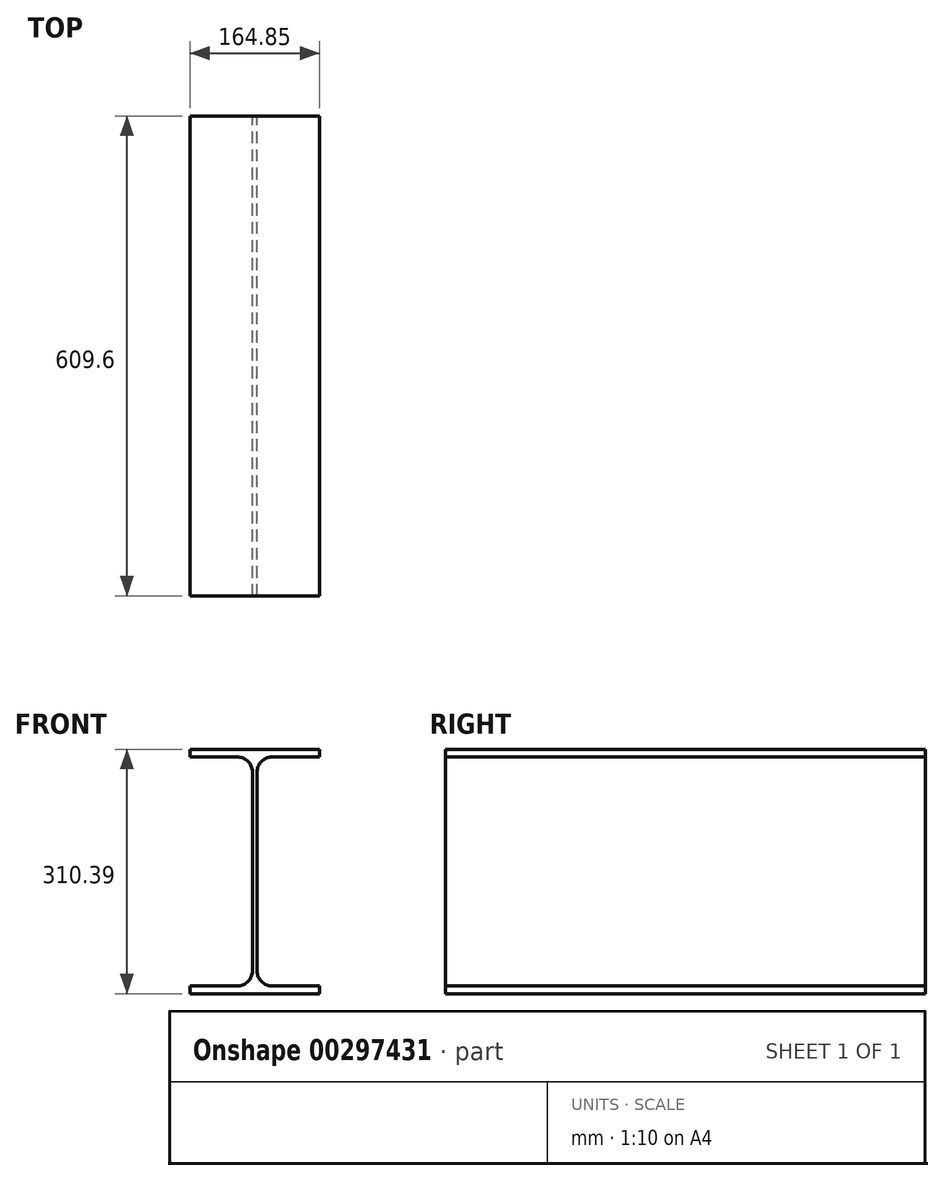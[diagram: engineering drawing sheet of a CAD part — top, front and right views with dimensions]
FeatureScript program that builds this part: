
annotation { "Feature Type Name" : "Feature", "Feature Type Description" : "" }
export const myFeature = defineFeature(function(context is Context, id is Id, definition is map)
    precondition{}
    {
        {
            var Q0;
            Q0=qCreatedBy(makeId("Front.planeOp"),FACE);
            var sketch = newSketch(context, id + "F0", { "sketchPlane" : qUnion([Q0])});
            skLineSegment(sketch, "E0", {"start": v(-2132.4, 1134.06) * mm, "end": v(-2031.56, 1134.06) * mm});
            skLineSegment(sketch, "E1", {"start": v(-2132.4, 1436.58) * mm, "end": v(-2031.56, 1436.58) * mm});
            skLineSegment(sketch, "E2", {"start": v(-2060.53, 1139.78) * mm, "end": v(-2031.56, 1139.78) * mm});
            skLineSegment(sketch, "E3", {"start": v(-2060.53, 1430.86) * mm, "end": v(-2031.56, 1430.86) * mm});
            skLineSegment(sketch, "E4", {"start": v(-2084.52, 1158.69) * mm, "end": v(-2084.52, 1411.95) * mm});
            skLineSegment(sketch, "E5", {"start": v(-2079.44, 1158.69) * mm, "end": v(-2079.44, 1411.95) * mm});
            skArc(sketch, "E6", {"start": v(-2103.42, 1139.78) * mm, "mid": v(-2090.05, 1145.32) * mm, "end": v(-2084.52, 1158.69) * mm});
            skLineSegment(sketch, "E7", {"start": v(-2132.4, 1134.06) * mm, "end": v(-2132.4, 1139.78) * mm});
            skLineSegment(sketch, "E8", {"start": v(-2132.4, 1139.78) * mm, "end": v(-2103.42, 1139.78) * mm});
            skArc(sketch, "E9", {"start": v(-2079.44, 1158.69) * mm, "mid": v(-2073.9, 1145.32) * mm, "end": v(-2060.53, 1139.78) * mm});
            skArc(sketch, "E10", {"start": v(-2084.52, 1411.95) * mm, "mid": v(-2090.05, 1425.32) * mm, "end": v(-2103.42, 1430.86) * mm});
            skLineSegment(sketch, "E11", {"start": v(-2132.4, 1430.86) * mm, "end": v(-2103.42, 1430.86) * mm});
            skLineSegment(sketch, "E12", {"start": v(-2132.4, 1436.58) * mm, "end": v(-2132.4, 1430.86) * mm});
            skArc(sketch, "E13", {"start": v(-2060.53, 1430.86) * mm, "mid": v(-2073.9, 1425.32) * mm, "end": v(-2079.44, 1411.95) * mm});
            skLineSegment(sketch, "E14", {"start": v(-2031.56, 1134.06) * mm, "end": v(-2031.56, 1139.78) * mm});
            skLineSegment(sketch, "E15", {"start": v(-2031.56, 1436.58) * mm, "end": v(-2031.56, 1430.86) * mm});
            skLineSegment(sketch, "E16", {"start": v(-2100.87, 1115.17) * mm, "end": v(-2063.08, 1152.96) * mm});
            skLineSegment(sketch, "E17", {"start": v(-2100.87, 1152.96) * mm, "end": v(-2063.08, 1115.17) * mm});
            skLineSegment(sketch, "E18", {"start": v(-1754.46, 1159.46) * mm, "end": v(-1754.46, 1134.06) * mm});
            skLineSegment(sketch, "E19", {"start": v(-1653.62, 1134.06) * mm, "end": v(-1653.62, 1159.46) * mm});
            skLineSegment(sketch, "E20", {"start": v(-1706.58, 1134.06) * mm, "end": v(-1706.58, 1159.46) * mm});
            skLineSegment(sketch, "E21", {"start": v(-1701.5, 1134.06) * mm, "end": v(-1701.5, 1159.46) * mm});
            skLineSegment(sketch, "E22", {"start": v(-1754.46, 1134.06) * mm, "end": v(-1653.62, 1134.06) * mm});
            skLineSegment(sketch, "E23", {"start": v(-1653.62, 1159.46) * mm, "end": v(-1754.46, 1159.46) * mm});
            skLineSegment(sketch, "E24", {"start": v(-1722.93, 1115.17) * mm, "end": v(-1685.14, 1152.96) * mm});
            skLineSegment(sketch, "E25", {"start": v(-1722.93, 1152.96) * mm, "end": v(-1685.14, 1115.17) * mm});
            skLineSegment(sketch, "E26", {"start": v(-1338.77, 1430.86) * mm, "end": v(-1313.37, 1430.86) * mm});
            skLineSegment(sketch, "E27", {"start": v(-1338.77, 1139.78) * mm, "end": v(-1313.37, 1139.78) * mm});
            skLineSegment(sketch, "E28", {"start": v(-1313.37, 1436.58) * mm, "end": v(-1338.77, 1436.58) * mm});
            skLineSegment(sketch, "E29", {"start": v(-1338.77, 1134.06) * mm, "end": v(-1313.37, 1134.06) * mm});
            skLineSegment(sketch, "E30", {"start": v(-1338.77, 1436.58) * mm, "end": v(-1338.77, 1134.06) * mm});
            skLineSegment(sketch, "E31", {"start": v(-1313.37, 1134.06) * mm, "end": v(-1313.37, 1436.58) * mm});
            skLineSegment(sketch, "E32", {"start": v(-1357.67, 1115.17) * mm, "end": v(-1319.87, 1152.96) * mm});
            skLineSegment(sketch, "E33", {"start": v(-1357.67, 1152.96) * mm, "end": v(-1319.87, 1115.17) * mm});
            skLineSegment(sketch, "E34", {"start": v(-998.8, 1134.06) * mm, "end": v(-897.45, 1134.06) * mm});
            skLineSegment(sketch, "E35", {"start": v(-998.8, 1438.6) * mm, "end": v(-897.45, 1438.6) * mm});
            skArc(sketch, "E36", {"start": v(-945.33, 1159.83) * mm, "mid": v(-939.75, 1146.37) * mm, "end": v(-926.3, 1140.8) * mm});
            skArc(sketch, "E37", {"start": v(-926.3, 1431.88) * mm, "mid": v(-939.75, 1426.3) * mm, "end": v(-945.33, 1412.84) * mm});
            skLineSegment(sketch, "E38", {"start": v(-950.91, 1159.83) * mm, "end": v(-950.91, 1412.84) * mm});
            skLineSegment(sketch, "E39", {"start": v(-945.33, 1159.83) * mm, "end": v(-945.33, 1412.84) * mm});
            skLineSegment(sketch, "E40", {"start": v(-998.8, 1140.8) * mm, "end": v(-969.95, 1140.8) * mm});
            skLineSegment(sketch, "E41", {"start": v(-998.8, 1134.06) * mm, "end": v(-998.8, 1140.8) * mm});
            skArc(sketch, "E42", {"start": v(-969.95, 1140.8) * mm, "mid": v(-956.49, 1146.37) * mm, "end": v(-950.91, 1159.83) * mm});
            skLineSegment(sketch, "E43", {"start": v(-998.8, 1431.88) * mm, "end": v(-969.95, 1431.88) * mm});
            skLineSegment(sketch, "E44", {"start": v(-998.8, 1438.6) * mm, "end": v(-998.8, 1431.88) * mm});
            skArc(sketch, "E45", {"start": v(-950.91, 1412.84) * mm, "mid": v(-956.49, 1426.3) * mm, "end": v(-969.95, 1431.88) * mm});
            skLineSegment(sketch, "E46", {"start": v(-926.3, 1140.8) * mm, "end": v(-897.45, 1140.8) * mm});
            skLineSegment(sketch, "E47", {"start": v(-897.45, 1134.06) * mm, "end": v(-897.45, 1140.8) * mm});
            skLineSegment(sketch, "E48", {"start": v(-926.3, 1431.88) * mm, "end": v(-897.45, 1431.88) * mm});
            skLineSegment(sketch, "E49", {"start": v(-897.45, 1438.6) * mm, "end": v(-897.45, 1431.88) * mm});
            skLineSegment(sketch, "E50", {"start": v(-967.02, 1115.17) * mm, "end": v(-929.22, 1152.96) * mm});
            skLineSegment(sketch, "E51", {"start": v(-967.02, 1152.96) * mm, "end": v(-929.22, 1115.17) * mm});
            skLineSegment(sketch, "E52", {"start": v(-519.74, 1159.46) * mm, "end": v(-620.57, 1159.46) * mm});
            skLineSegment(sketch, "E53", {"start": v(-620.57, 1134.06) * mm, "end": v(-519.74, 1134.06) * mm});
            skLineSegment(sketch, "E54", {"start": v(-620.57, 1159.46) * mm, "end": v(-620.57, 1134.06) * mm});
            skLineSegment(sketch, "E55", {"start": v(-572.95, 1134.06) * mm, "end": v(-572.95, 1159.46) * mm});
            skLineSegment(sketch, "E56", {"start": v(-567.36, 1134.06) * mm, "end": v(-567.36, 1159.46) * mm});
            skLineSegment(sketch, "E57", {"start": v(-519.74, 1134.06) * mm, "end": v(-519.74, 1159.46) * mm});
            skLineSegment(sketch, "E58", {"start": v(-589.05, 1115.17) * mm, "end": v(-551.26, 1152.96) * mm});
            skLineSegment(sketch, "E59", {"start": v(-589.05, 1152.96) * mm, "end": v(-551.26, 1115.17) * mm});
            skLineSegment(sketch, "E60", {"start": v(-204.92, 1438.6) * mm, "end": v(-204.92, 1134.06) * mm});
            skLineSegment(sketch, "E61", {"start": v(-179.52, 1134.06) * mm, "end": v(-179.52, 1438.6) * mm});
            skLineSegment(sketch, "E62", {"start": v(-204.92, 1140.8) * mm, "end": v(-179.52, 1140.8) * mm});
            skLineSegment(sketch, "E63", {"start": v(-204.92, 1134.06) * mm, "end": v(-179.52, 1134.06) * mm});
            skLineSegment(sketch, "E64", {"start": v(-204.92, 1431.88) * mm, "end": v(-179.52, 1431.88) * mm});
            skLineSegment(sketch, "E65", {"start": v(-179.52, 1438.6) * mm, "end": v(-204.92, 1438.6) * mm});
            skLineSegment(sketch, "E66", {"start": v(-223.81, 1115.17) * mm, "end": v(-186.02, 1152.96) * mm});
            skLineSegment(sketch, "E67", {"start": v(-223.81, 1152.96) * mm, "end": v(-186.02, 1115.17) * mm});
            skLineSegment(sketch, "E68", {"start": v(134.87, 1134.06) * mm, "end": v(236.6, 1134.06) * mm});
            skLineSegment(sketch, "E69", {"start": v(134.87, 1442.93) * mm, "end": v(236.6, 1442.93) * mm});
            skArc(sketch, "E70", {"start": v(188.72, 1162.26) * mm, "mid": v(194.37, 1148.6) * mm, "end": v(208.02, 1142.95) * mm});
            skArc(sketch, "E71", {"start": v(208.02, 1434.04) * mm, "mid": v(194.37, 1428.38) * mm, "end": v(188.72, 1414.73) * mm});
            skLineSegment(sketch, "E72", {"start": v(182.75, 1162.26) * mm, "end": v(182.75, 1414.73) * mm});
            skLineSegment(sketch, "E73", {"start": v(188.72, 1162.26) * mm, "end": v(188.72, 1414.73) * mm});
            skLineSegment(sketch, "E74", {"start": v(134.87, 1142.95) * mm, "end": v(163.45, 1142.95) * mm});
            skLineSegment(sketch, "E75", {"start": v(134.87, 1134.06) * mm, "end": v(134.87, 1142.95) * mm});
            skArc(sketch, "E76", {"start": v(163.45, 1142.95) * mm, "mid": v(177.1, 1148.6) * mm, "end": v(182.75, 1162.26) * mm});
            skLineSegment(sketch, "E77", {"start": v(134.87, 1434.04) * mm, "end": v(163.45, 1434.04) * mm});
            skLineSegment(sketch, "E78", {"start": v(134.87, 1442.93) * mm, "end": v(134.87, 1434.04) * mm});
            skArc(sketch, "E79", {"start": v(182.75, 1414.73) * mm, "mid": v(177.1, 1428.38) * mm, "end": v(163.45, 1434.04) * mm});
            skLineSegment(sketch, "E80", {"start": v(208.02, 1142.95) * mm, "end": v(236.6, 1142.95) * mm});
            skLineSegment(sketch, "E81", {"start": v(236.6, 1134.06) * mm, "end": v(236.6, 1142.95) * mm});
            skLineSegment(sketch, "E82", {"start": v(208.02, 1434.04) * mm, "end": v(236.6, 1434.04) * mm});
            skLineSegment(sketch, "E83", {"start": v(236.6, 1442.93) * mm, "end": v(236.6, 1434.04) * mm});
            skLineSegment(sketch, "E84", {"start": v(166.84, 1115.17) * mm, "end": v(204.63, 1152.96) * mm});
            skLineSegment(sketch, "E85", {"start": v(166.84, 1152.96) * mm, "end": v(204.63, 1115.17) * mm});
            skLineSegment(sketch, "E86", {"start": v(614.12, 1134.06) * mm, "end": v(614.12, 1159.46) * mm});
            skLineSegment(sketch, "E87", {"start": v(561.16, 1134.06) * mm, "end": v(561.16, 1159.46) * mm});
            skLineSegment(sketch, "E88", {"start": v(566.24, 1134.06) * mm, "end": v(566.24, 1159.46) * mm});
            skLineSegment(sketch, "E89", {"start": v(513.28, 1159.46) * mm, "end": v(513.28, 1134.06) * mm});
            skLineSegment(sketch, "E90", {"start": v(513.28, 1134.06) * mm, "end": v(614.12, 1134.06) * mm});
            skLineSegment(sketch, "E91", {"start": v(614.12, 1159.46) * mm, "end": v(513.28, 1159.46) * mm});
            skLineSegment(sketch, "E92", {"start": v(544.8, 1115.17) * mm, "end": v(582.6, 1152.96) * mm});
            skLineSegment(sketch, "E93", {"start": v(544.8, 1152.96) * mm, "end": v(582.6, 1115.17) * mm});
            skLineSegment(sketch, "E94", {"start": v(928.94, 1134.06) * mm, "end": v(954.34, 1134.06) * mm});
            skLineSegment(sketch, "E95", {"start": v(954.34, 1436.58) * mm, "end": v(928.94, 1436.58) * mm});
            skLineSegment(sketch, "E96", {"start": v(928.94, 1139.78) * mm, "end": v(954.34, 1139.78) * mm});
            skLineSegment(sketch, "E97", {"start": v(928.94, 1430.86) * mm, "end": v(954.34, 1430.86) * mm});
            skLineSegment(sketch, "E98", {"start": v(928.94, 1436.58) * mm, "end": v(928.94, 1134.06) * mm});
            skLineSegment(sketch, "E99", {"start": v(954.34, 1134.06) * mm, "end": v(954.34, 1436.58) * mm});
            skLineSegment(sketch, "E100", {"start": v(910.04, 1115.17) * mm, "end": v(947.84, 1152.96) * mm});
            skLineSegment(sketch, "E101", {"start": v(910.04, 1152.96) * mm, "end": v(947.84, 1115.17) * mm});
            skLineSegment(sketch, "E102", {"start": v(1268.41, 1134.06) * mm, "end": v(1370.77, 1134.06) * mm});
            skLineSegment(sketch, "E103", {"start": v(1268.41, 1446.74) * mm, "end": v(1370.77, 1446.74) * mm});
            skArc(sketch, "E104", {"start": v(1322.9, 1164.4) * mm, "mid": v(1328.62, 1150.58) * mm, "end": v(1342.44, 1144.86) * mm});
            skArc(sketch, "E105", {"start": v(1342.44, 1435.94) * mm, "mid": v(1328.62, 1430.22) * mm, "end": v(1322.9, 1416.4) * mm});
            skLineSegment(sketch, "E106", {"start": v(1316.3, 1164.4) * mm, "end": v(1316.3, 1416.4) * mm});
            skLineSegment(sketch, "E107", {"start": v(1322.9, 1164.4) * mm, "end": v(1322.9, 1416.4) * mm});
            skLineSegment(sketch, "E108", {"start": v(1268.41, 1144.86) * mm, "end": v(1296.75, 1144.86) * mm});
            skLineSegment(sketch, "E109", {"start": v(1268.41, 1134.06) * mm, "end": v(1268.41, 1144.86) * mm});
            skArc(sketch, "E110", {"start": v(1296.75, 1144.86) * mm, "mid": v(1310.57, 1150.58) * mm, "end": v(1316.3, 1164.4) * mm});
            skLineSegment(sketch, "E111", {"start": v(1268.41, 1435.94) * mm, "end": v(1296.75, 1435.94) * mm});
            skLineSegment(sketch, "E112", {"start": v(1268.41, 1446.74) * mm, "end": v(1268.41, 1435.94) * mm});
            skArc(sketch, "E113", {"start": v(1316.3, 1416.4) * mm, "mid": v(1310.57, 1430.22) * mm, "end": v(1296.75, 1435.94) * mm});
            skLineSegment(sketch, "E114", {"start": v(1370.77, 1134.06) * mm, "end": v(1370.77, 1144.86) * mm});
            skLineSegment(sketch, "E115", {"start": v(1342.44, 1144.86) * mm, "end": v(1370.77, 1144.86) * mm});
            skLineSegment(sketch, "E116", {"start": v(1342.44, 1435.94) * mm, "end": v(1370.77, 1435.94) * mm});
            skLineSegment(sketch, "E117", {"start": v(1370.77, 1446.74) * mm, "end": v(1370.77, 1435.94) * mm});
            skLineSegment(sketch, "E118", {"start": v(1300.7, 1115.17) * mm, "end": v(1338.5, 1152.96) * mm});
            skLineSegment(sketch, "E119", {"start": v(1300.7, 1152.96) * mm, "end": v(1338.5, 1115.17) * mm});
            skLineSegment(sketch, "E120", {"start": v(1747.95, 1134.06) * mm, "end": v(1747.95, 1159.46) * mm});
            skLineSegment(sketch, "E121", {"start": v(1647.11, 1159.46) * mm, "end": v(1647.11, 1134.06) * mm});
            skLineSegment(sketch, "E122", {"start": v(1694.74, 1134.06) * mm, "end": v(1694.74, 1159.46) * mm});
            skLineSegment(sketch, "E123", {"start": v(1700.33, 1134.06) * mm, "end": v(1700.33, 1159.46) * mm});
            skLineSegment(sketch, "E124", {"start": v(1647.11, 1134.06) * mm, "end": v(1747.95, 1134.06) * mm});
            skLineSegment(sketch, "E125", {"start": v(1747.95, 1159.46) * mm, "end": v(1647.11, 1159.46) * mm});
            skLineSegment(sketch, "E126", {"start": v(1678.63, 1115.17) * mm, "end": v(1716.43, 1152.96) * mm});
            skLineSegment(sketch, "E127", {"start": v(1678.63, 1152.96) * mm, "end": v(1716.43, 1115.17) * mm});
            skLineSegment(sketch, "E128", {"start": v(2062.8, 1134.06) * mm, "end": v(2088.2, 1134.06) * mm});
            skLineSegment(sketch, "E129", {"start": v(2062.8, 1140.8) * mm, "end": v(2088.2, 1140.8) * mm});
            skLineSegment(sketch, "E130", {"start": v(2088.2, 1438.6) * mm, "end": v(2062.8, 1438.6) * mm});
            skLineSegment(sketch, "E131", {"start": v(2062.8, 1431.88) * mm, "end": v(2088.2, 1431.88) * mm});
            skLineSegment(sketch, "E132", {"start": v(2062.8, 1438.6) * mm, "end": v(2062.8, 1134.06) * mm});
            skLineSegment(sketch, "E133", {"start": v(2088.2, 1134.06) * mm, "end": v(2088.2, 1438.6) * mm});
            skLineSegment(sketch, "E134", {"start": v(2043.9, 1115.17) * mm, "end": v(2081.7, 1152.96) * mm});
            skLineSegment(sketch, "E135", {"start": v(2043.9, 1152.96) * mm, "end": v(2081.7, 1115.17) * mm});
            skLineSegment(sketch, "E136", {"start": v(-2164.4, 555.25) * mm, "end": v(-1999.55, 555.25) * mm});
            skLineSegment(sketch, "E137", {"start": v(-2164.4, 865.64) * mm, "end": v(-1999.55, 865.64) * mm});
            skLineSegment(sketch, "E138", {"start": v(-2059.66, 564.9) * mm, "end": v(-1999.55, 564.9) * mm});
            skLineSegment(sketch, "E139", {"start": v(-2059.66, 855.98) * mm, "end": v(-1999.55, 855.98) * mm});
            skLineSegment(sketch, "E140", {"start": v(-2084.9, 584.3) * mm, "end": v(-2084.9, 836.58) * mm});
            skLineSegment(sketch, "E141", {"start": v(-2079.05, 584.3) * mm, "end": v(-2079.05, 836.58) * mm});
            skLineSegment(sketch, "E142", {"start": v(-2164.4, 564.9) * mm, "end": v(-2104.3, 564.9) * mm});
            skLineSegment(sketch, "E143", {"start": v(-2164.4, 555.25) * mm, "end": v(-2164.4, 564.9) * mm});
            skArc(sketch, "E144", {"start": v(-2104.3, 564.9) * mm, "mid": v(-2090.58, 570.58) * mm, "end": v(-2084.9, 584.3) * mm});
            skArc(sketch, "E145", {"start": v(-2079.05, 584.3) * mm, "mid": v(-2073.37, 570.58) * mm, "end": v(-2059.66, 564.9) * mm});
            skLineSegment(sketch, "E146", {"start": v(-2164.4, 855.98) * mm, "end": v(-2104.3, 855.98) * mm});
            skLineSegment(sketch, "E147", {"start": v(-2164.4, 865.64) * mm, "end": v(-2164.4, 855.98) * mm});
            skArc(sketch, "E148", {"start": v(-2084.9, 836.58) * mm, "mid": v(-2090.58, 850.3) * mm, "end": v(-2104.3, 855.98) * mm});
            skArc(sketch, "E149", {"start": v(-2059.66, 855.98) * mm, "mid": v(-2073.37, 850.3) * mm, "end": v(-2079.05, 836.58) * mm});
            skLineSegment(sketch, "E150", {"start": v(-1999.55, 555.25) * mm, "end": v(-1999.55, 564.9) * mm});
            skLineSegment(sketch, "E151", {"start": v(-1999.55, 865.64) * mm, "end": v(-1999.55, 855.98) * mm});
            skLineSegment(sketch, "E152", {"start": v(-2100.87, 536.35) * mm, "end": v(-2063.08, 574.15) * mm});
            skLineSegment(sketch, "E153", {"start": v(-2100.87, 574.15) * mm, "end": v(-2063.08, 536.35) * mm});
            skLineSegment(sketch, "E154", {"start": v(-1653.17, 555.25) * mm, "end": v(-1653.17, 580.65) * mm});
            skLineSegment(sketch, "E155", {"start": v(-1707.02, 555.25) * mm, "end": v(-1707.02, 580.65) * mm});
            skLineSegment(sketch, "E156", {"start": v(-1701.05, 555.25) * mm, "end": v(-1701.05, 580.65) * mm});
            skLineSegment(sketch, "E157", {"start": v(-1754.9, 580.65) * mm, "end": v(-1754.9, 555.25) * mm});
            skLineSegment(sketch, "E158", {"start": v(-1754.9, 555.25) * mm, "end": v(-1653.17, 555.25) * mm});
            skLineSegment(sketch, "E159", {"start": v(-1653.17, 580.65) * mm, "end": v(-1754.9, 580.65) * mm});
            skLineSegment(sketch, "E160", {"start": v(-1722.93, 536.35) * mm, "end": v(-1685.14, 574.15) * mm});
            skLineSegment(sketch, "E161", {"start": v(-1722.93, 574.15) * mm, "end": v(-1685.14, 536.35) * mm});
            skLineSegment(sketch, "E162", {"start": v(-1338.77, 555.25) * mm, "end": v(-1313.37, 555.25) * mm});
            skLineSegment(sketch, "E163", {"start": v(-1313.37, 864.11) * mm, "end": v(-1338.77, 864.11) * mm});
            skLineSegment(sketch, "E164", {"start": v(-1338.77, 564.14) * mm, "end": v(-1313.37, 564.14) * mm});
            skLineSegment(sketch, "E165", {"start": v(-1338.77, 855.22) * mm, "end": v(-1313.37, 855.22) * mm});
            skLineSegment(sketch, "E166", {"start": v(-1338.77, 864.11) * mm, "end": v(-1338.77, 555.25) * mm});
            skLineSegment(sketch, "E167", {"start": v(-1313.37, 555.25) * mm, "end": v(-1313.37, 864.11) * mm});
            skLineSegment(sketch, "E168", {"start": v(-1357.67, 536.35) * mm, "end": v(-1319.87, 574.15) * mm});
            skLineSegment(sketch, "E169", {"start": v(-1357.67, 574.15) * mm, "end": v(-1319.87, 536.35) * mm});
            skLineSegment(sketch, "E170", {"start": v(-1030.92, 555.25) * mm, "end": v(-865.32, 555.25) * mm});
            skLineSegment(sketch, "E171", {"start": v(-1030.92, 868.68) * mm, "end": v(-865.32, 868.68) * mm});
            skLineSegment(sketch, "E172", {"start": v(-1030.92, 566.42) * mm, "end": v(-971.01, 566.42) * mm});
            skLineSegment(sketch, "E173", {"start": v(-1030.92, 857.5) * mm, "end": v(-971.01, 857.5) * mm});
            skLineSegment(sketch, "E174", {"start": v(-1030.92, 555.25) * mm, "end": v(-1030.92, 566.42) * mm});
            skLineSegment(sketch, "E175", {"start": v(-1030.92, 868.68) * mm, "end": v(-1030.92, 857.5) * mm});
            skLineSegment(sketch, "E176", {"start": v(-951.42, 586.01) * mm, "end": v(-951.42, 837.92) * mm});
            skLineSegment(sketch, "E177", {"start": v(-944.82, 586.01) * mm, "end": v(-944.82, 837.92) * mm});
            skLineSegment(sketch, "E178", {"start": v(-925.23, 566.42) * mm, "end": v(-865.32, 566.42) * mm});
            skArc(sketch, "E179", {"start": v(-944.82, 586.01) * mm, "mid": v(-939.08, 572.16) * mm, "end": v(-925.23, 566.42) * mm});
            skArc(sketch, "E180", {"start": v(-971.01, 566.42) * mm, "mid": v(-957.16, 572.16) * mm, "end": v(-951.42, 586.01) * mm});
            skLineSegment(sketch, "E181", {"start": v(-865.32, 555.25) * mm, "end": v(-865.32, 566.42) * mm});
            skLineSegment(sketch, "E182", {"start": v(-925.23, 857.5) * mm, "end": v(-865.32, 857.5) * mm});
            skArc(sketch, "E183", {"start": v(-925.23, 857.5) * mm, "mid": v(-939.08, 851.77) * mm, "end": v(-944.82, 837.92) * mm});
            skArc(sketch, "E184", {"start": v(-951.42, 837.92) * mm, "mid": v(-957.16, 851.77) * mm, "end": v(-971.01, 857.5) * mm});
            skLineSegment(sketch, "E185", {"start": v(-865.32, 868.68) * mm, "end": v(-865.32, 857.5) * mm});
            skLineSegment(sketch, "E186", {"start": v(-967.02, 536.35) * mm, "end": v(-929.22, 574.15) * mm});
            skLineSegment(sketch, "E187", {"start": v(-967.02, 574.15) * mm, "end": v(-929.22, 536.35) * mm});
            skLineSegment(sketch, "E188", {"start": v(-621.03, 580.65) * mm, "end": v(-621.03, 555.25) * mm});
            skLineSegment(sketch, "E189", {"start": v(-573.47, 555.25) * mm, "end": v(-573.47, 580.65) * mm});
            skLineSegment(sketch, "E190", {"start": v(-566.87, 555.25) * mm, "end": v(-566.87, 580.65) * mm});
            skLineSegment(sketch, "E191", {"start": v(-519.3, 555.25) * mm, "end": v(-519.3, 580.65) * mm});
            skLineSegment(sketch, "E192", {"start": v(-621.03, 555.25) * mm, "end": v(-519.3, 555.25) * mm});
            skLineSegment(sketch, "E193", {"start": v(-519.3, 580.65) * mm, "end": v(-621.03, 580.65) * mm});
            skLineSegment(sketch, "E194", {"start": v(-589.07, 536.35) * mm, "end": v(-551.27, 574.15) * mm});
            skLineSegment(sketch, "E195", {"start": v(-589.07, 574.15) * mm, "end": v(-551.27, 536.35) * mm});
            skLineSegment(sketch, "E196", {"start": v(-204.92, 555.25) * mm, "end": v(-179.52, 555.25) * mm});
            skLineSegment(sketch, "E197", {"start": v(-204.92, 566.04) * mm, "end": v(-179.52, 566.04) * mm});
            skLineSegment(sketch, "E198", {"start": v(-179.52, 867.92) * mm, "end": v(-204.92, 867.92) * mm});
            skLineSegment(sketch, "E199", {"start": v(-204.92, 857.13) * mm, "end": v(-179.52, 857.13) * mm});
            skLineSegment(sketch, "E200", {"start": v(-204.92, 867.92) * mm, "end": v(-204.92, 555.25) * mm});
            skLineSegment(sketch, "E201", {"start": v(-179.52, 555.25) * mm, "end": v(-179.52, 867.92) * mm});
            skLineSegment(sketch, "E202", {"start": v(-223.81, 536.35) * mm, "end": v(-186.02, 574.15) * mm});
            skLineSegment(sketch, "E203", {"start": v(-223.81, 574.15) * mm, "end": v(-186.02, 536.35) * mm});
            skLineSegment(sketch, "E204", {"start": v(102.42, 555.25) * mm, "end": v(269.05, 555.25) * mm});
            skLineSegment(sketch, "E205", {"start": v(102.42, 872.75) * mm, "end": v(269.05, 872.75) * mm});
            skArc(sketch, "E206", {"start": v(162.08, 568.46) * mm, "mid": v(176.11, 574.27) * mm, "end": v(181.93, 588.3) * mm});
            skArc(sketch, "E207", {"start": v(181.93, 839.7) * mm, "mid": v(176.11, 853.73) * mm, "end": v(162.08, 859.54) * mm});
            skLineSegment(sketch, "E208", {"start": v(102.42, 568.46) * mm, "end": v(162.08, 568.46) * mm});
            skLineSegment(sketch, "E209", {"start": v(102.42, 555.25) * mm, "end": v(102.42, 568.46) * mm});
            skLineSegment(sketch, "E210", {"start": v(102.42, 859.54) * mm, "end": v(162.08, 859.54) * mm});
            skLineSegment(sketch, "E211", {"start": v(102.42, 872.75) * mm, "end": v(102.42, 859.54) * mm});
            skLineSegment(sketch, "E212", {"start": v(181.93, 588.3) * mm, "end": v(181.93, 839.7) * mm});
            skLineSegment(sketch, "E213", {"start": v(189.55, 588.3) * mm, "end": v(189.55, 839.7) * mm});
            skLineSegment(sketch, "E214", {"start": v(209.4, 568.46) * mm, "end": v(269.05, 568.46) * mm});
            skArc(sketch, "E215", {"start": v(189.55, 588.3) * mm, "mid": v(195.36, 574.27) * mm, "end": v(209.4, 568.46) * mm});
            skLineSegment(sketch, "E216", {"start": v(269.05, 555.25) * mm, "end": v(269.05, 568.46) * mm});
            skLineSegment(sketch, "E217", {"start": v(209.4, 859.54) * mm, "end": v(269.05, 859.54) * mm});
            skArc(sketch, "E218", {"start": v(209.4, 859.54) * mm, "mid": v(195.36, 853.73) * mm, "end": v(189.55, 839.7) * mm});
            skLineSegment(sketch, "E219", {"start": v(269.05, 872.75) * mm, "end": v(269.05, 859.54) * mm});
            skLineSegment(sketch, "E220", {"start": v(166.84, 536.35) * mm, "end": v(204.63, 574.15) * mm});
            skLineSegment(sketch, "E221", {"start": v(166.84, 574.15) * mm, "end": v(204.63, 536.35) * mm});
            skLineSegment(sketch, "E222", {"start": v(647, 555.25) * mm, "end": v(647, 580.65) * mm});
            skLineSegment(sketch, "E223", {"start": v(480.38, 580.65) * mm, "end": v(480.38, 555.25) * mm});
            skLineSegment(sketch, "E224", {"start": v(559.88, 555.25) * mm, "end": v(559.88, 580.65) * mm});
            skLineSegment(sketch, "E225", {"start": v(567.5, 555.25) * mm, "end": v(567.5, 580.65) * mm});
            skLineSegment(sketch, "E226", {"start": v(480.38, 555.25) * mm, "end": v(647, 555.25) * mm});
            skLineSegment(sketch, "E227", {"start": v(647, 580.65) * mm, "end": v(480.38, 580.65) * mm});
            skLineSegment(sketch, "E228", {"start": v(544.8, 536.35) * mm, "end": v(582.59, 574.15) * mm});
            skLineSegment(sketch, "E229", {"start": v(544.8, 574.15) * mm, "end": v(582.59, 536.35) * mm});
            skLineSegment(sketch, "E230", {"start": v(928.94, 555.25) * mm, "end": v(954.34, 555.25) * mm});
            skLineSegment(sketch, "E231", {"start": v(954.34, 872.75) * mm, "end": v(928.94, 872.75) * mm});
            skLineSegment(sketch, "E232", {"start": v(928.94, 568.46) * mm, "end": v(954.34, 568.46) * mm});
            skLineSegment(sketch, "E233", {"start": v(928.94, 859.54) * mm, "end": v(954.34, 859.54) * mm});
            skLineSegment(sketch, "E234", {"start": v(928.94, 872.75) * mm, "end": v(928.94, 555.25) * mm});
            skLineSegment(sketch, "E235", {"start": v(954.34, 555.25) * mm, "end": v(954.34, 872.75) * mm});
            skLineSegment(sketch, "E236", {"start": v(910.04, 536.35) * mm, "end": v(947.84, 574.15) * mm});
            skLineSegment(sketch, "E237", {"start": v(910.04, 574.15) * mm, "end": v(947.84, 536.35) * mm});
            skLineSegment(sketch, "E238", {"start": v(1217.93, 555.25) * mm, "end": v(1421.26, 555.25) * mm});
            skLineSegment(sketch, "E239", {"start": v(1217.93, 858.52) * mm, "end": v(1421.26, 858.52) * mm});
            skArc(sketch, "E240", {"start": v(1296.9, 568.33) * mm, "mid": v(1310.3, 573.88) * mm, "end": v(1315.85, 587.28) * mm});
            skArc(sketch, "E241", {"start": v(1315.85, 826.49) * mm, "mid": v(1310.3, 839.9) * mm, "end": v(1296.9, 845.44) * mm});
            skLineSegment(sketch, "E242", {"start": v(1315.85, 587.28) * mm, "end": v(1315.85, 826.49) * mm});
            skLineSegment(sketch, "E243", {"start": v(1217.93, 568.33) * mm, "end": v(1296.9, 568.33) * mm});
            skLineSegment(sketch, "E244", {"start": v(1217.93, 555.25) * mm, "end": v(1217.93, 568.33) * mm});
            skLineSegment(sketch, "E245", {"start": v(1217.93, 845.44) * mm, "end": v(1296.9, 845.44) * mm});
            skLineSegment(sketch, "E246", {"start": v(1217.93, 858.52) * mm, "end": v(1217.93, 845.44) * mm});
            skLineSegment(sketch, "E247", {"start": v(1323.34, 587.28) * mm, "end": v(1323.34, 826.49) * mm});
            skLineSegment(sketch, "E248", {"start": v(1342.3, 568.33) * mm, "end": v(1421.26, 568.33) * mm});
            skArc(sketch, "E249", {"start": v(1323.34, 587.28) * mm, "mid": v(1328.9, 573.88) * mm, "end": v(1342.3, 568.33) * mm});
            skLineSegment(sketch, "E250", {"start": v(1421.26, 555.25) * mm, "end": v(1421.26, 568.33) * mm});
            skLineSegment(sketch, "E251", {"start": v(1342.3, 845.44) * mm, "end": v(1421.26, 845.44) * mm});
            skArc(sketch, "E252", {"start": v(1342.3, 845.44) * mm, "mid": v(1328.9, 839.9) * mm, "end": v(1323.34, 826.49) * mm});
            skLineSegment(sketch, "E253", {"start": v(1421.26, 858.52) * mm, "end": v(1421.26, 845.44) * mm});
            skLineSegment(sketch, "E254", {"start": v(1300.7, 536.35) * mm, "end": v(1338.5, 574.15) * mm});
            skLineSegment(sketch, "E255", {"start": v(1300.7, 574.15) * mm, "end": v(1338.5, 536.35) * mm});
            skLineSegment(sketch, "E256", {"start": v(1799.26, 555.25) * mm, "end": v(1799.26, 580.65) * mm});
            skLineSegment(sketch, "E257", {"start": v(1595.8, 580.65) * mm, "end": v(1595.8, 555.25) * mm});
            skLineSegment(sketch, "E258", {"start": v(1693.79, 555.25) * mm, "end": v(1693.79, 580.65) * mm});
            skLineSegment(sketch, "E259", {"start": v(1701.28, 555.25) * mm, "end": v(1701.28, 580.65) * mm});
            skLineSegment(sketch, "E260", {"start": v(1595.8, 555.25) * mm, "end": v(1799.26, 555.25) * mm});
            skLineSegment(sketch, "E261", {"start": v(1799.26, 580.65) * mm, "end": v(1595.8, 580.65) * mm});
            skLineSegment(sketch, "E262", {"start": v(1678.63, 536.35) * mm, "end": v(1716.43, 574.15) * mm});
            skLineSegment(sketch, "E263", {"start": v(1678.63, 574.15) * mm, "end": v(1716.43, 536.35) * mm});
            skLineSegment(sketch, "E264", {"start": v(2088.2, 858.52) * mm, "end": v(2062.8, 858.52) * mm});
            skLineSegment(sketch, "E265", {"start": v(2062.8, 845.44) * mm, "end": v(2088.2, 845.44) * mm});
            skLineSegment(sketch, "E266", {"start": v(2062.8, 555.25) * mm, "end": v(2088.2, 555.25) * mm});
            skLineSegment(sketch, "E267", {"start": v(2062.8, 568.33) * mm, "end": v(2088.2, 568.33) * mm});
            skLineSegment(sketch, "E268", {"start": v(2062.8, 858.52) * mm, "end": v(2062.8, 555.25) * mm});
            skLineSegment(sketch, "E269", {"start": v(2088.2, 555.25) * mm, "end": v(2088.2, 858.52) * mm});
            skLineSegment(sketch, "E270", {"start": v(2043.9, 536.35) * mm, "end": v(2081.7, 574.15) * mm});
            skLineSegment(sketch, "E271", {"start": v(2043.9, 574.15) * mm, "end": v(2081.7, 536.35) * mm});
            skLineSegment(sketch, "E272", {"start": v(-2184.15, -23.57) * mm, "end": v(-1979.8, -23.57) * mm});
            skLineSegment(sketch, "E273", {"start": v(-2184.15, 282.76) * mm, "end": v(-1979.8, 282.76) * mm});
            skArc(sketch, "E274", {"start": v(-2105.38, -8.96) * mm, "mid": v(-2091.84, -3.35) * mm, "end": v(-2086.23, 10.18) * mm});
            skArc(sketch, "E275", {"start": v(-2086.23, 249) * mm, "mid": v(-2091.84, 262.54) * mm, "end": v(-2105.38, 268.15) * mm});
            skLineSegment(sketch, "E276", {"start": v(-2184.15, -8.96) * mm, "end": v(-2105.38, -8.96) * mm});
            skLineSegment(sketch, "E277", {"start": v(-2184.15, -23.57) * mm, "end": v(-2184.15, -8.96) * mm});
            skLineSegment(sketch, "E278", {"start": v(-2184.15, 268.15) * mm, "end": v(-2105.38, 268.15) * mm});
            skLineSegment(sketch, "E279", {"start": v(-2184.15, 282.76) * mm, "end": v(-2184.15, 268.15) * mm});
            skLineSegment(sketch, "E280", {"start": v(-2086.23, 10.18) * mm, "end": v(-2086.23, 249) * mm});
            skLineSegment(sketch, "E281", {"start": v(-2077.72, 10.18) * mm, "end": v(-2077.72, 249) * mm});
            skLineSegment(sketch, "E282", {"start": v(-2058.58, -8.96) * mm, "end": v(-1979.8, -8.96) * mm});
            skArc(sketch, "E283", {"start": v(-2077.72, 10.18) * mm, "mid": v(-2072.11, -3.35) * mm, "end": v(-2058.58, -8.96) * mm});
            skLineSegment(sketch, "E284", {"start": v(-1979.8, -23.57) * mm, "end": v(-1979.8, -8.96) * mm});
            skLineSegment(sketch, "E285", {"start": v(-2058.58, 268.15) * mm, "end": v(-1979.8, 268.15) * mm});
            skArc(sketch, "E286", {"start": v(-2058.58, 268.15) * mm, "mid": v(-2072.11, 262.54) * mm, "end": v(-2077.72, 249) * mm});
            skLineSegment(sketch, "E287", {"start": v(-1979.8, 282.76) * mm, "end": v(-1979.8, 268.15) * mm});
            skLineSegment(sketch, "E288", {"start": v(-2100.87, -42.47) * mm, "end": v(-2063.08, -4.67) * mm});
            skLineSegment(sketch, "E289", {"start": v(-2100.87, -4.67) * mm, "end": v(-2063.08, -42.47) * mm});
            skLineSegment(sketch, "E290", {"start": v(-1601.85, 1.83) * mm, "end": v(-1806.2, 1.83) * mm});
            skLineSegment(sketch, "E291", {"start": v(-1806.2, -23.57) * mm, "end": v(-1601.85, -23.57) * mm});
            skLineSegment(sketch, "E292", {"start": v(-1806.2, 1.83) * mm, "end": v(-1806.2, -23.57) * mm});
            skLineSegment(sketch, "E293", {"start": v(-1708.28, -23.57) * mm, "end": v(-1708.28, 1.83) * mm});
            skLineSegment(sketch, "E294", {"start": v(-1699.77, -23.57) * mm, "end": v(-1699.77, 1.83) * mm});
            skLineSegment(sketch, "E295", {"start": v(-1601.85, -23.57) * mm, "end": v(-1601.85, 1.83) * mm});
            skLineSegment(sketch, "E296", {"start": v(-1722.92, -42.47) * mm, "end": v(-1685.13, -4.67) * mm});
            skLineSegment(sketch, "E297", {"start": v(-1722.92, -4.67) * mm, "end": v(-1685.13, -42.47) * mm});
            skLineSegment(sketch, "E298", {"start": v(-1313.37, -23.57) * mm, "end": v(-1313.37, 282.76) * mm});
            skLineSegment(sketch, "E299", {"start": v(-1338.77, 282.76) * mm, "end": v(-1338.77, -23.57) * mm});
            skLineSegment(sketch, "E300", {"start": v(-1338.77, -23.57) * mm, "end": v(-1313.37, -23.57) * mm});
            skLineSegment(sketch, "E301", {"start": v(-1338.77, -8.96) * mm, "end": v(-1313.37, -8.96) * mm});
            skLineSegment(sketch, "E302", {"start": v(-1313.37, 282.76) * mm, "end": v(-1338.77, 282.76) * mm});
            skLineSegment(sketch, "E303", {"start": v(-1338.77, 268.15) * mm, "end": v(-1313.37, 268.15) * mm});
            skLineSegment(sketch, "E304", {"start": v(-1357.67, -42.47) * mm, "end": v(-1319.87, -4.67) * mm});
            skLineSegment(sketch, "E305", {"start": v(-1357.67, -4.67) * mm, "end": v(-1319.87, -42.47) * mm});
            skLineSegment(sketch, "E306", {"start": v(-1050.74, -23.57) * mm, "end": v(-845.5, -23.57) * mm});
            skLineSegment(sketch, "E307", {"start": v(-1050.74, 286.06) * mm, "end": v(-845.5, 286.06) * mm});
            skArc(sketch, "E308", {"start": v(-943.42, 12.04) * mm, "mid": v(-937.75, -1.64) * mm, "end": v(-924.07, -7.31) * mm});
            skArc(sketch, "E309", {"start": v(-924.07, 269.8) * mm, "mid": v(-937.75, 264.13) * mm, "end": v(-943.42, 250.45) * mm});
            skLineSegment(sketch, "E310", {"start": v(-952.82, 12.04) * mm, "end": v(-952.82, 250.45) * mm});
            skLineSegment(sketch, "E311", {"start": v(-943.42, 12.04) * mm, "end": v(-943.42, 250.45) * mm});
            skLineSegment(sketch, "E312", {"start": v(-1050.74, -7.31) * mm, "end": v(-972.17, -7.31) * mm});
            skLineSegment(sketch, "E313", {"start": v(-1050.74, -23.57) * mm, "end": v(-1050.74, -7.31) * mm});
            skArc(sketch, "E314", {"start": v(-972.17, -7.31) * mm, "mid": v(-958.49, -1.64) * mm, "end": v(-952.82, 12.04) * mm});
            skLineSegment(sketch, "E315", {"start": v(-1050.74, 269.8) * mm, "end": v(-972.17, 269.8) * mm});
            skLineSegment(sketch, "E316", {"start": v(-1050.74, 286.06) * mm, "end": v(-1050.74, 269.8) * mm});
            skArc(sketch, "E317", {"start": v(-952.82, 250.45) * mm, "mid": v(-958.49, 264.13) * mm, "end": v(-972.17, 269.8) * mm});
            skLineSegment(sketch, "E318", {"start": v(-924.07, -7.31) * mm, "end": v(-845.5, -7.31) * mm});
            skLineSegment(sketch, "E319", {"start": v(-845.5, -23.57) * mm, "end": v(-845.5, -7.31) * mm});
            skLineSegment(sketch, "E320", {"start": v(-924.07, 269.8) * mm, "end": v(-845.5, 269.8) * mm});
            skLineSegment(sketch, "E321", {"start": v(-845.5, 286.06) * mm, "end": v(-845.5, 269.8) * mm});
            skLineSegment(sketch, "E322", {"start": v(-967.02, -42.47) * mm, "end": v(-929.22, -4.67) * mm});
            skLineSegment(sketch, "E323", {"start": v(-967.02, -4.67) * mm, "end": v(-929.22, -42.47) * mm});
            skLineSegment(sketch, "E324", {"start": v(-468, -23.57) * mm, "end": v(-468, 1.83) * mm});
            skLineSegment(sketch, "E325", {"start": v(-672.34, 1.83) * mm, "end": v(-672.34, -23.57) * mm});
            skLineSegment(sketch, "E326", {"start": v(-574.87, -23.57) * mm, "end": v(-574.87, 1.83) * mm});
            skLineSegment(sketch, "E327", {"start": v(-565.47, -23.57) * mm, "end": v(-565.47, 1.83) * mm});
            skLineSegment(sketch, "E328", {"start": v(-672.34, -23.57) * mm, "end": v(-468, -23.57) * mm});
            skLineSegment(sketch, "E329", {"start": v(-468, 1.83) * mm, "end": v(-672.34, 1.83) * mm});
            skLineSegment(sketch, "E330", {"start": v(-589.07, -42.47) * mm, "end": v(-551.27, -4.67) * mm});
            skLineSegment(sketch, "E331", {"start": v(-589.07, -4.67) * mm, "end": v(-551.27, -42.47) * mm});
            skLineSegment(sketch, "E332", {"start": v(-204.92, 269.8) * mm, "end": v(-179.52, 269.8) * mm});
            skLineSegment(sketch, "E333", {"start": v(-179.52, 286.06) * mm, "end": v(-204.92, 286.06) * mm});
            skLineSegment(sketch, "E334", {"start": v(-204.92, -7.31) * mm, "end": v(-179.52, -7.31) * mm});
            skLineSegment(sketch, "E335", {"start": v(-204.92, -23.57) * mm, "end": v(-179.52, -23.57) * mm});
            skLineSegment(sketch, "E336", {"start": v(-204.92, 286.06) * mm, "end": v(-204.92, -23.57) * mm});
            skLineSegment(sketch, "E337", {"start": v(-179.52, -23.57) * mm, "end": v(-179.52, 286.06) * mm});
            skLineSegment(sketch, "E338", {"start": v(-223.81, -42.47) * mm, "end": v(-186.02, -4.67) * mm});
            skLineSegment(sketch, "E339", {"start": v(-223.81, -4.67) * mm, "end": v(-186.02, -42.47) * mm});
            skLineSegment(sketch, "E340", {"start": v(58.8, -23.57) * mm, "end": v(312.67, -23.57) * mm});
            skLineSegment(sketch, "E341", {"start": v(58.8, 282.76) * mm, "end": v(312.67, 282.76) * mm});
            skArc(sketch, "E342", {"start": v(190.12, 10.18) * mm, "mid": v(195.73, -3.35) * mm, "end": v(209.26, -8.96) * mm});
            skArc(sketch, "E343", {"start": v(209.26, 268.15) * mm, "mid": v(195.73, 262.54) * mm, "end": v(190.12, 249) * mm});
            skLineSegment(sketch, "E344", {"start": v(181.35, 10.18) * mm, "end": v(181.35, 249) * mm});
            skLineSegment(sketch, "E345", {"start": v(190.12, 10.18) * mm, "end": v(190.12, 249) * mm});
            skLineSegment(sketch, "E346", {"start": v(58.8, -8.96) * mm, "end": v(162.2, -8.96) * mm});
            skLineSegment(sketch, "E347", {"start": v(58.8, -23.57) * mm, "end": v(58.8, -8.96) * mm});
            skArc(sketch, "E348", {"start": v(162.2, -8.96) * mm, "mid": v(175.75, -3.35) * mm, "end": v(181.35, 10.18) * mm});
            skLineSegment(sketch, "E349", {"start": v(58.8, 268.15) * mm, "end": v(162.2, 268.15) * mm});
            skLineSegment(sketch, "E350", {"start": v(58.8, 282.76) * mm, "end": v(58.8, 268.15) * mm});
            skArc(sketch, "E351", {"start": v(181.35, 249) * mm, "mid": v(175.75, 262.54) * mm, "end": v(162.2, 268.15) * mm});
            skLineSegment(sketch, "E352", {"start": v(209.26, -8.96) * mm, "end": v(312.67, -8.96) * mm});
            skLineSegment(sketch, "E353", {"start": v(312.67, -23.57) * mm, "end": v(312.67, -8.96) * mm});
            skLineSegment(sketch, "E354", {"start": v(209.26, 268.15) * mm, "end": v(312.67, 268.15) * mm});
            skLineSegment(sketch, "E355", {"start": v(312.67, 282.76) * mm, "end": v(312.67, 268.15) * mm});
            skLineSegment(sketch, "E356", {"start": v(166.84, -42.47) * mm, "end": v(204.63, -4.67) * mm});
            skLineSegment(sketch, "E357", {"start": v(166.84, -4.67) * mm, "end": v(204.63, -42.47) * mm});
            skLineSegment(sketch, "E358", {"start": v(690.62, -23.54) * mm, "end": v(690.62, 1.86) * mm});
            skLineSegment(sketch, "E359", {"start": v(559.3, -23.54) * mm, "end": v(559.3, 1.86) * mm});
            skLineSegment(sketch, "E360", {"start": v(568.07, -23.54) * mm, "end": v(568.07, 1.86) * mm});
            skLineSegment(sketch, "E361", {"start": v(436.75, 1.86) * mm, "end": v(436.75, -23.54) * mm});
            skLineSegment(sketch, "E362", {"start": v(436.75, -23.54) * mm, "end": v(690.62, -23.54) * mm});
            skLineSegment(sketch, "E363", {"start": v(690.62, 1.86) * mm, "end": v(436.75, 1.86) * mm});
            skLineSegment(sketch, "E364", {"start": v(544.8, -42.44) * mm, "end": v(582.59, -4.64) * mm});
            skLineSegment(sketch, "E365", {"start": v(544.8, -4.64) * mm, "end": v(582.59, -42.44) * mm});
            skLineSegment(sketch, "E366", {"start": v(954.35, 282.76) * mm, "end": v(928.95, 282.76) * mm});
            skLineSegment(sketch, "E367", {"start": v(928.95, 268.15) * mm, "end": v(954.35, 268.15) * mm});
            skLineSegment(sketch, "E368", {"start": v(928.95, -23.57) * mm, "end": v(954.35, -23.57) * mm});
            skLineSegment(sketch, "E369", {"start": v(928.95, -8.96) * mm, "end": v(954.35, -8.96) * mm});
            skLineSegment(sketch, "E370", {"start": v(928.95, 282.76) * mm, "end": v(928.95, -23.57) * mm});
            skLineSegment(sketch, "E371", {"start": v(954.35, -23.57) * mm, "end": v(954.35, 282.76) * mm});
            skLineSegment(sketch, "E372", {"start": v(910.06, -42.47) * mm, "end": v(947.85, -4.67) * mm});
            skLineSegment(sketch, "E373", {"start": v(910.06, -4.67) * mm, "end": v(947.85, -42.47) * mm});
            skLineSegment(sketch, "E374", {"start": v(1192.47, -23.54) * mm, "end": v(1446.72, -23.54) * mm});
            skLineSegment(sketch, "E375", {"start": v(1192.47, 286.08) * mm, "end": v(1446.72, 286.08) * mm});
            skArc(sketch, "E376", {"start": v(1324.16, 12.07) * mm, "mid": v(1329.83, -1.62) * mm, "end": v(1343.52, -7.29) * mm});
            skArc(sketch, "E377", {"start": v(1343.52, 269.83) * mm, "mid": v(1329.83, 264.16) * mm, "end": v(1324.16, 250.48) * mm});
            skLineSegment(sketch, "E378", {"start": v(1315.02, 12.07) * mm, "end": v(1315.02, 250.48) * mm});
            skLineSegment(sketch, "E379", {"start": v(1324.16, 12.07) * mm, "end": v(1324.16, 250.48) * mm});
            skLineSegment(sketch, "E380", {"start": v(1192.47, -7.29) * mm, "end": v(1295.67, -7.29) * mm});
            skLineSegment(sketch, "E381", {"start": v(1192.47, -23.54) * mm, "end": v(1192.47, -7.29) * mm});
            skArc(sketch, "E382", {"start": v(1295.67, -7.29) * mm, "mid": v(1309.35, -1.62) * mm, "end": v(1315.02, 12.07) * mm});
            skLineSegment(sketch, "E383", {"start": v(1192.47, 269.83) * mm, "end": v(1295.67, 269.83) * mm});
            skLineSegment(sketch, "E384", {"start": v(1192.47, 286.08) * mm, "end": v(1192.47, 269.83) * mm});
            skArc(sketch, "E385", {"start": v(1315.02, 250.48) * mm, "mid": v(1309.35, 264.16) * mm, "end": v(1295.67, 269.83) * mm});
            skLineSegment(sketch, "E386", {"start": v(1343.52, -7.29) * mm, "end": v(1446.72, -7.29) * mm});
            skLineSegment(sketch, "E387", {"start": v(1446.72, -23.54) * mm, "end": v(1446.72, -7.29) * mm});
            skLineSegment(sketch, "E388", {"start": v(1343.52, 269.83) * mm, "end": v(1446.72, 269.83) * mm});
            skLineSegment(sketch, "E389", {"start": v(1446.72, 286.08) * mm, "end": v(1446.72, 269.83) * mm});
            skLineSegment(sketch, "E390", {"start": v(1300.7, -42.44) * mm, "end": v(1338.5, -4.64) * mm});
            skLineSegment(sketch, "E391", {"start": v(1300.7, -4.64) * mm, "end": v(1338.5, -42.44) * mm});
            skLineSegment(sketch, "E392", {"start": v(1824.47, -23.57) * mm, "end": v(1824.47, 1.83) * mm});
            skLineSegment(sketch, "E393", {"start": v(1570.6, 1.83) * mm, "end": v(1570.6, -23.57) * mm});
            skLineSegment(sketch, "E394", {"start": v(1692.96, -23.57) * mm, "end": v(1692.96, 1.83) * mm});
            skLineSegment(sketch, "E395", {"start": v(1702.1, -23.57) * mm, "end": v(1702.1, 1.83) * mm});
            skLineSegment(sketch, "E396", {"start": v(1570.6, -23.57) * mm, "end": v(1824.47, -23.57) * mm});
            skLineSegment(sketch, "E397", {"start": v(1824.47, 1.83) * mm, "end": v(1570.6, 1.83) * mm});
            skLineSegment(sketch, "E398", {"start": v(1678.63, -42.47) * mm, "end": v(1716.43, -4.67) * mm});
            skLineSegment(sketch, "E399", {"start": v(1678.63, -4.67) * mm, "end": v(1716.43, -42.47) * mm});
            skLineSegment(sketch, "E400", {"start": v(2088.18, -23.57) * mm, "end": v(2088.18, 286.06) * mm});
            skLineSegment(sketch, "E401", {"start": v(2062.78, 286.06) * mm, "end": v(2062.78, -23.57) * mm});
            skLineSegment(sketch, "E402", {"start": v(2062.78, -23.57) * mm, "end": v(2088.18, -23.57) * mm});
            skLineSegment(sketch, "E403", {"start": v(2062.78, -7.31) * mm, "end": v(2088.18, -7.31) * mm});
            skLineSegment(sketch, "E404", {"start": v(2088.18, 286.06) * mm, "end": v(2062.78, 286.06) * mm});
            skLineSegment(sketch, "E405", {"start": v(2062.78, 269.8) * mm, "end": v(2088.18, 269.8) * mm});
            skLineSegment(sketch, "E406", {"start": v(2043.89, -42.47) * mm, "end": v(2081.68, -4.67) * mm});
            skLineSegment(sketch, "E407", {"start": v(2043.89, -4.67) * mm, "end": v(2081.68, -42.47) * mm});
            skLineSegment(sketch, "E408", {"start": v(-2234.39, -602.36) * mm, "end": v(-1929.59, -602.36) * mm});
            skLineSegment(sketch, "E409", {"start": v(-2234.39, -294.5) * mm, "end": v(-1929.59, -294.5) * mm});
            skArc(sketch, "E410", {"start": v(-2106.18, -587) * mm, "mid": v(-2092.58, -581.35) * mm, "end": v(-2086.94, -567.75) * mm});
            skArc(sketch, "E411", {"start": v(-2086.94, -329.12) * mm, "mid": v(-2092.58, -315.51) * mm, "end": v(-2106.18, -309.88) * mm});
            skLineSegment(sketch, "E412", {"start": v(-2086.94, -567.75) * mm, "end": v(-2086.94, -329.12) * mm});
            skLineSegment(sketch, "E413", {"start": v(-2234.39, -587) * mm, "end": v(-2106.18, -587) * mm});
            skLineSegment(sketch, "E414", {"start": v(-2234.39, -602.36) * mm, "end": v(-2234.39, -587) * mm});
            skLineSegment(sketch, "E415", {"start": v(-2234.39, -309.88) * mm, "end": v(-2106.18, -309.88) * mm});
            skLineSegment(sketch, "E416", {"start": v(-2234.39, -294.5) * mm, "end": v(-2234.39, -309.88) * mm});
            skLineSegment(sketch, "E417", {"start": v(-2077.04, -567.75) * mm, "end": v(-2077.04, -329.12) * mm});
            skLineSegment(sketch, "E418", {"start": v(-2057.8, -587) * mm, "end": v(-1929.59, -587) * mm});
            skArc(sketch, "E419", {"start": v(-2077.04, -567.75) * mm, "mid": v(-2071.4, -581.35) * mm, "end": v(-2057.8, -587) * mm});
            skLineSegment(sketch, "E420", {"start": v(-1929.59, -602.36) * mm, "end": v(-1929.59, -587) * mm});
            skLineSegment(sketch, "E421", {"start": v(-2057.8, -309.88) * mm, "end": v(-1929.59, -309.88) * mm});
            skArc(sketch, "E422", {"start": v(-2057.8, -309.88) * mm, "mid": v(-2071.4, -315.51) * mm, "end": v(-2077.04, -329.12) * mm});
            skLineSegment(sketch, "E423", {"start": v(-1929.59, -294.5) * mm, "end": v(-1929.59, -309.88) * mm});
            skLineSegment(sketch, "E424", {"start": v(-2100.89, -621.25) * mm, "end": v(-2063.1, -583.46) * mm});
            skLineSegment(sketch, "E425", {"start": v(-2100.89, -583.46) * mm, "end": v(-2063.1, -621.25) * mm});
            skLineSegment(sketch, "E426", {"start": v(-1551.62, -602.38) * mm, "end": v(-1551.62, -576.98) * mm});
            skLineSegment(sketch, "E427", {"start": v(-1708.98, -602.38) * mm, "end": v(-1708.98, -576.98) * mm});
            skLineSegment(sketch, "E428", {"start": v(-1699.07, -602.38) * mm, "end": v(-1699.07, -576.98) * mm});
            skLineSegment(sketch, "E429", {"start": v(-1856.42, -576.98) * mm, "end": v(-1856.42, -602.38) * mm});
            skLineSegment(sketch, "E430", {"start": v(-1856.42, -602.38) * mm, "end": v(-1551.62, -602.38) * mm});
            skLineSegment(sketch, "E431", {"start": v(-1551.62, -576.98) * mm, "end": v(-1856.42, -576.98) * mm});
            skLineSegment(sketch, "E432", {"start": v(-1722.92, -621.28) * mm, "end": v(-1685.13, -583.49) * mm});
            skLineSegment(sketch, "E433", {"start": v(-1722.92, -583.49) * mm, "end": v(-1685.13, -621.28) * mm});
            skLineSegment(sketch, "E434", {"start": v(-1313.37, -602.36) * mm, "end": v(-1313.37, -294.5) * mm});
            skLineSegment(sketch, "E435", {"start": v(-1338.77, -294.5) * mm, "end": v(-1338.77, -602.36) * mm});
            skLineSegment(sketch, "E436", {"start": v(-1338.77, -602.36) * mm, "end": v(-1313.37, -602.36) * mm});
            skLineSegment(sketch, "E437", {"start": v(-1338.77, -587) * mm, "end": v(-1313.37, -587) * mm});
            skLineSegment(sketch, "E438", {"start": v(-1313.37, -294.5) * mm, "end": v(-1338.77, -294.5) * mm});
            skLineSegment(sketch, "E439", {"start": v(-1338.77, -309.88) * mm, "end": v(-1313.37, -309.88) * mm});
            skLineSegment(sketch, "E440", {"start": v(-1357.67, -621.25) * mm, "end": v(-1319.87, -583.46) * mm});
            skLineSegment(sketch, "E441", {"start": v(-1357.67, -583.46) * mm, "end": v(-1319.87, -621.25) * mm});
            skLineSegment(sketch, "E442", {"start": v(-1101.03, -602.36) * mm, "end": v(-795.21, -602.36) * mm});
            skLineSegment(sketch, "E443", {"start": v(-1101.03, -291.2) * mm, "end": v(-795.21, -291.2) * mm});
            skArc(sketch, "E444", {"start": v(-973.03, -585.34) * mm, "mid": v(-959.28, -579.64) * mm, "end": v(-953.58, -565.9) * mm});
            skArc(sketch, "E445", {"start": v(-953.58, -327.67) * mm, "mid": v(-959.28, -313.92) * mm, "end": v(-973.03, -308.23) * mm});
            skLineSegment(sketch, "E446", {"start": v(-1101.03, -585.34) * mm, "end": v(-973.03, -585.34) * mm});
            skLineSegment(sketch, "E447", {"start": v(-1101.03, -602.36) * mm, "end": v(-1101.03, -585.34) * mm});
            skLineSegment(sketch, "E448", {"start": v(-1101.03, -308.23) * mm, "end": v(-973.03, -308.23) * mm});
            skLineSegment(sketch, "E449", {"start": v(-1101.03, -291.2) * mm, "end": v(-1101.03, -308.23) * mm});
            skLineSegment(sketch, "E450", {"start": v(-953.58, -565.9) * mm, "end": v(-953.58, -327.67) * mm});
            skLineSegment(sketch, "E451", {"start": v(-942.66, -565.9) * mm, "end": v(-942.66, -327.67) * mm});
            skLineSegment(sketch, "E452", {"start": v(-923.21, -585.34) * mm, "end": v(-795.21, -585.34) * mm});
            skArc(sketch, "E453", {"start": v(-942.66, -565.9) * mm, "mid": v(-936.96, -579.64) * mm, "end": v(-923.21, -585.34) * mm});
            skLineSegment(sketch, "E454", {"start": v(-795.21, -602.36) * mm, "end": v(-795.21, -585.34) * mm});
            skLineSegment(sketch, "E455", {"start": v(-923.21, -308.23) * mm, "end": v(-795.21, -308.23) * mm});
            skArc(sketch, "E456", {"start": v(-923.21, -308.23) * mm, "mid": v(-936.96, -313.92) * mm, "end": v(-942.66, -327.67) * mm});
            skLineSegment(sketch, "E457", {"start": v(-795.21, -291.2) * mm, "end": v(-795.21, -308.23) * mm});
            skLineSegment(sketch, "E458", {"start": v(-967.02, -621.25) * mm, "end": v(-929.22, -583.46) * mm});
            skLineSegment(sketch, "E459", {"start": v(-967.02, -583.46) * mm, "end": v(-929.22, -621.25) * mm});
            skLineSegment(sketch, "E460", {"start": v(-417.77, -602.38) * mm, "end": v(-417.77, -576.98) * mm});
            skLineSegment(sketch, "E461", {"start": v(-575.63, -602.38) * mm, "end": v(-575.63, -576.98) * mm});
            skLineSegment(sketch, "E462", {"start": v(-564.7, -602.38) * mm, "end": v(-564.7, -576.98) * mm});
            skLineSegment(sketch, "E463", {"start": v(-722.57, -576.98) * mm, "end": v(-722.57, -602.38) * mm});
            skLineSegment(sketch, "E464", {"start": v(-722.57, -602.38) * mm, "end": v(-417.77, -602.38) * mm});
            skLineSegment(sketch, "E465", {"start": v(-417.77, -576.98) * mm, "end": v(-722.57, -576.98) * mm});
            skLineSegment(sketch, "E466", {"start": v(-589.07, -621.28) * mm, "end": v(-551.27, -583.49) * mm});
            skLineSegment(sketch, "E467", {"start": v(-589.07, -583.49) * mm, "end": v(-551.27, -621.28) * mm});
            skLineSegment(sketch, "E468", {"start": v(-179.53, -602.36) * mm, "end": v(-179.53, -291.2) * mm});
            skLineSegment(sketch, "E469", {"start": v(-204.93, -291.2) * mm, "end": v(-204.93, -602.36) * mm});
            skLineSegment(sketch, "E470", {"start": v(-204.93, -602.36) * mm, "end": v(-179.53, -602.36) * mm});
            skLineSegment(sketch, "E471", {"start": v(-204.93, -585.34) * mm, "end": v(-179.53, -585.34) * mm});
            skLineSegment(sketch, "E472", {"start": v(-179.53, -291.2) * mm, "end": v(-204.93, -291.2) * mm});
            skLineSegment(sketch, "E473", {"start": v(-204.93, -308.23) * mm, "end": v(-179.53, -308.23) * mm});
            skLineSegment(sketch, "E474", {"start": v(-223.83, -621.25) * mm, "end": v(-186.03, -583.46) * mm});
            skLineSegment(sketch, "E475", {"start": v(-223.83, -583.46) * mm, "end": v(-186.03, -621.25) * mm});
            skLineSegment(sketch, "E476", {"start": v(32.32, -602.38) * mm, "end": v(339.15, -602.38) * mm});
            skLineSegment(sketch, "E477", {"start": v(32.32, -287.93) * mm, "end": v(339.15, -287.93) * mm});
            skLineSegment(sketch, "E478", {"start": v(211.36, -583.71) * mm, "end": v(339.15, -583.71) * mm});
            skLineSegment(sketch, "E479", {"start": v(211.36, -306.6) * mm, "end": v(339.15, -306.6) * mm});
            skLineSegment(sketch, "E480", {"start": v(179.77, -564.06) * mm, "end": v(179.77, -326.25) * mm});
            skLineSegment(sketch, "E481", {"start": v(191.7, -564.06) * mm, "end": v(191.7, -326.25) * mm});
            skLineSegment(sketch, "E482", {"start": v(32.32, -583.71) * mm, "end": v(160.11, -583.71) * mm});
            skLineSegment(sketch, "E483", {"start": v(32.32, -602.38) * mm, "end": v(32.32, -583.71) * mm});
            skArc(sketch, "E484", {"start": v(160.11, -583.71) * mm, "mid": v(174.01, -577.96) * mm, "end": v(179.77, -564.06) * mm});
            skArc(sketch, "E485", {"start": v(191.7, -564.06) * mm, "mid": v(197.46, -577.96) * mm, "end": v(211.36, -583.71) * mm});
            skLineSegment(sketch, "E486", {"start": v(32.32, -306.6) * mm, "end": v(160.11, -306.6) * mm});
            skLineSegment(sketch, "E487", {"start": v(32.32, -287.93) * mm, "end": v(32.32, -306.6) * mm});
            skArc(sketch, "E488", {"start": v(179.77, -326.25) * mm, "mid": v(174.01, -312.36) * mm, "end": v(160.11, -306.6) * mm});
            skArc(sketch, "E489", {"start": v(211.36, -306.6) * mm, "mid": v(197.46, -312.36) * mm, "end": v(191.7, -326.25) * mm});
            skLineSegment(sketch, "E490", {"start": v(339.15, -602.38) * mm, "end": v(339.15, -583.71) * mm});
            skLineSegment(sketch, "E491", {"start": v(339.15, -287.93) * mm, "end": v(339.15, -306.6) * mm});
            skLineSegment(sketch, "E492", {"start": v(166.84, -621.28) * mm, "end": v(204.63, -583.49) * mm});
            skLineSegment(sketch, "E493", {"start": v(166.84, -583.49) * mm, "end": v(204.63, -621.28) * mm});
            skLineSegment(sketch, "E494", {"start": v(717.1, -576.98) * mm, "end": v(410.27, -576.98) * mm});
            skLineSegment(sketch, "E495", {"start": v(410.27, -602.38) * mm, "end": v(717.1, -602.38) * mm});
            skLineSegment(sketch, "E496", {"start": v(410.27, -576.98) * mm, "end": v(410.27, -602.38) * mm});
            skLineSegment(sketch, "E497", {"start": v(717.1, -602.38) * mm, "end": v(717.1, -576.98) * mm});
            skLineSegment(sketch, "E498", {"start": v(557.72, -602.38) * mm, "end": v(557.72, -576.98) * mm});
            skLineSegment(sketch, "E499", {"start": v(569.66, -602.38) * mm, "end": v(569.66, -576.98) * mm});
            skLineSegment(sketch, "E500", {"start": v(544.8, -621.28) * mm, "end": v(582.59, -583.49) * mm});
            skLineSegment(sketch, "E501", {"start": v(544.8, -583.49) * mm, "end": v(582.59, -621.28) * mm});
            skLineSegment(sketch, "E502", {"start": v(954.34, -287.9) * mm, "end": v(928.94, -287.9) * mm});
            skLineSegment(sketch, "E503", {"start": v(928.94, -306.57) * mm, "end": v(954.34, -306.57) * mm});
            skLineSegment(sketch, "E504", {"start": v(928.94, -602.36) * mm, "end": v(954.34, -602.36) * mm});
            skLineSegment(sketch, "E505", {"start": v(928.94, -583.69) * mm, "end": v(954.34, -583.69) * mm});
            skLineSegment(sketch, "E506", {"start": v(928.94, -287.9) * mm, "end": v(928.94, -602.36) * mm});
            skLineSegment(sketch, "E507", {"start": v(954.34, -602.36) * mm, "end": v(954.34, -287.9) * mm});
            skLineSegment(sketch, "E508", {"start": v(910.04, -621.25) * mm, "end": v(947.84, -583.46) * mm});
            skLineSegment(sketch, "E509", {"start": v(910.04, -583.46) * mm, "end": v(947.84, -621.25) * mm});
            skLineSegment(sketch, "E510", {"start": v(1165.6, -602.38) * mm, "end": v(1473.58, -602.38) * mm});
            skLineSegment(sketch, "E511", {"start": v(1165.6, -284.12) * mm, "end": v(1473.58, -284.12) * mm});
            skArc(sketch, "E512", {"start": v(1326.13, -561.92) * mm, "mid": v(1331.96, -575.98) * mm, "end": v(1346.02, -581.8) * mm});
            skArc(sketch, "E513", {"start": v(1346.02, -304.7) * mm, "mid": v(1331.96, -310.52) * mm, "end": v(1326.13, -324.59) * mm});
            skLineSegment(sketch, "E514", {"start": v(1313.05, -561.92) * mm, "end": v(1313.05, -324.59) * mm});
            skLineSegment(sketch, "E515", {"start": v(1326.13, -561.92) * mm, "end": v(1326.13, -324.59) * mm});
            skLineSegment(sketch, "E516", {"start": v(1165.6, -581.8) * mm, "end": v(1293.16, -581.8) * mm});
            skLineSegment(sketch, "E517", {"start": v(1165.6, -602.38) * mm, "end": v(1165.6, -581.8) * mm});
            skArc(sketch, "E518", {"start": v(1293.16, -581.8) * mm, "mid": v(1307.23, -575.98) * mm, "end": v(1313.05, -561.92) * mm});
            skLineSegment(sketch, "E519", {"start": v(1165.6, -304.7) * mm, "end": v(1293.16, -304.7) * mm});
            skLineSegment(sketch, "E520", {"start": v(1165.6, -284.12) * mm, "end": v(1165.6, -304.7) * mm});
            skArc(sketch, "E521", {"start": v(1313.05, -324.59) * mm, "mid": v(1307.23, -310.52) * mm, "end": v(1293.16, -304.7) * mm});
            skLineSegment(sketch, "E522", {"start": v(1346.02, -581.8) * mm, "end": v(1473.58, -581.8) * mm});
            skLineSegment(sketch, "E523", {"start": v(1473.58, -602.38) * mm, "end": v(1473.58, -581.8) * mm});
            skLineSegment(sketch, "E524", {"start": v(1346.02, -304.7) * mm, "end": v(1473.58, -304.7) * mm});
            skLineSegment(sketch, "E525", {"start": v(1473.58, -284.12) * mm, "end": v(1473.58, -304.7) * mm});
            skLineSegment(sketch, "E526", {"start": v(1300.7, -621.28) * mm, "end": v(1338.5, -583.49) * mm});
            skLineSegment(sketch, "E527", {"start": v(1300.7, -583.49) * mm, "end": v(1338.5, -621.28) * mm});
            skLineSegment(sketch, "E528", {"start": v(1850.97, -602.38) * mm, "end": v(1850.97, -576.98) * mm});
            skLineSegment(sketch, "E529", {"start": v(1691.02, -602.38) * mm, "end": v(1691.02, -576.98) * mm});
            skLineSegment(sketch, "E530", {"start": v(1704.1, -602.38) * mm, "end": v(1704.1, -576.98) * mm});
            skLineSegment(sketch, "E531", {"start": v(1544.14, -576.98) * mm, "end": v(1544.14, -602.38) * mm});
            skLineSegment(sketch, "E532", {"start": v(1544.14, -602.38) * mm, "end": v(1850.97, -602.38) * mm});
            skLineSegment(sketch, "E533", {"start": v(1850.97, -576.98) * mm, "end": v(1544.14, -576.98) * mm});
            skLineSegment(sketch, "E534", {"start": v(1678.66, -621.28) * mm, "end": v(1716.45, -583.49) * mm});
            skLineSegment(sketch, "E535", {"start": v(1678.66, -583.49) * mm, "end": v(1716.45, -621.28) * mm});
            skLineSegment(sketch, "E536", {"start": v(2088.2, -284.12) * mm, "end": v(2062.8, -284.12) * mm});
            skLineSegment(sketch, "E537", {"start": v(2062.8, -304.7) * mm, "end": v(2088.2, -304.7) * mm});
            skLineSegment(sketch, "E538", {"start": v(2062.8, -602.38) * mm, "end": v(2088.2, -602.38) * mm});
            skLineSegment(sketch, "E539", {"start": v(2062.8, -581.8) * mm, "end": v(2088.2, -581.8) * mm});
            skLineSegment(sketch, "E540", {"start": v(2062.8, -284.12) * mm, "end": v(2062.8, -602.38) * mm});
            skLineSegment(sketch, "E541", {"start": v(2088.2, -602.38) * mm, "end": v(2088.2, -284.12) * mm});
            skLineSegment(sketch, "E542", {"start": v(2043.91, -621.28) * mm, "end": v(2081.7, -583.49) * mm});
            skLineSegment(sketch, "E543", {"start": v(2043.91, -583.49) * mm, "end": v(2081.7, -621.28) * mm});
            skLineSegment(sketch, "E544", {"start": v(-2236.4, -1181.2) * mm, "end": v(-1927.54, -1181.2) * mm});
            skLineSegment(sketch, "E545", {"start": v(-2236.4, -858.36) * mm, "end": v(-1927.54, -858.36) * mm});
            skArc(sketch, "E546", {"start": v(-2109.14, -1158.34) * mm, "mid": v(-2094.87, -1152.43) * mm, "end": v(-2088.96, -1138.16) * mm});
            skArc(sketch, "E547", {"start": v(-2088.96, -901.4) * mm, "mid": v(-2094.87, -887.13) * mm, "end": v(-2109.14, -881.22) * mm});
            skLineSegment(sketch, "E548", {"start": v(-2088.96, -1138.16) * mm, "end": v(-2088.96, -901.4) * mm});
            skLineSegment(sketch, "E549", {"start": v(-2236.4, -1158.34) * mm, "end": v(-2109.14, -1158.34) * mm});
            skLineSegment(sketch, "E550", {"start": v(-2236.4, -1181.2) * mm, "end": v(-2236.4, -1158.34) * mm});
            skLineSegment(sketch, "E551", {"start": v(-2236.4, -881.22) * mm, "end": v(-2109.14, -881.22) * mm});
            skLineSegment(sketch, "E552", {"start": v(-2236.4, -858.36) * mm, "end": v(-2236.4, -881.22) * mm});
            skLineSegment(sketch, "E553", {"start": v(-2075, -1138.16) * mm, "end": v(-2075, -901.4) * mm});
            skLineSegment(sketch, "E554", {"start": v(-2054.81, -1158.34) * mm, "end": v(-1927.54, -1158.34) * mm});
            skArc(sketch, "E555", {"start": v(-2075, -1138.16) * mm, "mid": v(-2069.08, -1152.43) * mm, "end": v(-2054.81, -1158.34) * mm});
            skLineSegment(sketch, "E556", {"start": v(-1927.54, -1181.2) * mm, "end": v(-1927.54, -1158.34) * mm});
            skLineSegment(sketch, "E557", {"start": v(-2054.81, -881.22) * mm, "end": v(-1927.54, -881.22) * mm});
            skArc(sketch, "E558", {"start": v(-2054.81, -881.22) * mm, "mid": v(-2069.08, -887.13) * mm, "end": v(-2075, -901.4) * mm});
            skLineSegment(sketch, "E559", {"start": v(-1927.54, -858.36) * mm, "end": v(-1927.54, -881.22) * mm});
            skLineSegment(sketch, "E560", {"start": v(-2100.87, -1200.1) * mm, "end": v(-2063.08, -1162.3) * mm});
            skLineSegment(sketch, "E561", {"start": v(-2100.87, -1162.3) * mm, "end": v(-2063.08, -1200.1) * mm});
            skLineSegment(sketch, "E562", {"start": v(-1549.58, -1181.17) * mm, "end": v(-1549.58, -1155.77) * mm});
            skLineSegment(sketch, "E563", {"start": v(-1711, -1181.17) * mm, "end": v(-1711, -1155.77) * mm});
            skLineSegment(sketch, "E564", {"start": v(-1697.03, -1181.17) * mm, "end": v(-1697.03, -1155.77) * mm});
            skLineSegment(sketch, "E565", {"start": v(-1858.44, -1155.77) * mm, "end": v(-1858.44, -1181.17) * mm});
            skLineSegment(sketch, "E566", {"start": v(-1858.44, -1181.17) * mm, "end": v(-1549.58, -1181.17) * mm});
            skLineSegment(sketch, "E567", {"start": v(-1549.58, -1155.77) * mm, "end": v(-1858.44, -1155.77) * mm});
            skLineSegment(sketch, "E568", {"start": v(-1722.9, -1200.07) * mm, "end": v(-1685.11, -1162.27) * mm});
            skLineSegment(sketch, "E569", {"start": v(-1722.9, -1162.27) * mm, "end": v(-1685.11, -1200.07) * mm});
            skLineSegment(sketch, "E570", {"start": v(-1313.37, -1181.2) * mm, "end": v(-1313.37, -858.36) * mm});
            skLineSegment(sketch, "E571", {"start": v(-1338.77, -858.36) * mm, "end": v(-1338.77, -1181.2) * mm});
            skLineSegment(sketch, "E572", {"start": v(-1338.77, -1181.2) * mm, "end": v(-1313.37, -1181.2) * mm});
            skLineSegment(sketch, "E573", {"start": v(-1338.77, -1158.34) * mm, "end": v(-1313.37, -1158.34) * mm});
            skLineSegment(sketch, "E574", {"start": v(-1313.37, -858.36) * mm, "end": v(-1338.77, -858.36) * mm});
            skLineSegment(sketch, "E575", {"start": v(-1338.77, -881.22) * mm, "end": v(-1313.37, -881.22) * mm});
            skLineSegment(sketch, "E576", {"start": v(-1357.67, -1200.1) * mm, "end": v(-1319.87, -1162.3) * mm});
            skLineSegment(sketch, "E577", {"start": v(-1357.67, -1162.3) * mm, "end": v(-1319.87, -1200.1) * mm});
            skLineSegment(sketch, "E578", {"start": v(-1103.31, -1181.2) * mm, "end": v(-792.93, -1181.2) * mm});
            skLineSegment(sketch, "E579", {"start": v(-1103.31, -853.8) * mm, "end": v(-792.93, -853.8) * mm});
            skArc(sketch, "E580", {"start": v(-940.37, -1135.59) * mm, "mid": v(-934.38, -1150.06) * mm, "end": v(-919.9, -1156.05) * mm});
            skArc(sketch, "E581", {"start": v(-919.9, -878.94) * mm, "mid": v(-934.38, -884.93) * mm, "end": v(-940.37, -899.4) * mm});
            skLineSegment(sketch, "E582", {"start": v(-955.87, -1135.59) * mm, "end": v(-955.87, -899.4) * mm});
            skLineSegment(sketch, "E583", {"start": v(-940.37, -1135.59) * mm, "end": v(-940.37, -899.4) * mm});
            skLineSegment(sketch, "E584", {"start": v(-1103.31, -1156.05) * mm, "end": v(-976.33, -1156.05) * mm});
            skLineSegment(sketch, "E585", {"start": v(-1103.31, -1181.2) * mm, "end": v(-1103.31, -1156.05) * mm});
            skArc(sketch, "E586", {"start": v(-976.33, -1156.05) * mm, "mid": v(-961.86, -1150.06) * mm, "end": v(-955.87, -1135.59) * mm});
            skLineSegment(sketch, "E587", {"start": v(-1103.31, -878.94) * mm, "end": v(-976.33, -878.94) * mm});
            skLineSegment(sketch, "E588", {"start": v(-1103.31, -853.8) * mm, "end": v(-1103.31, -878.94) * mm});
            skArc(sketch, "E589", {"start": v(-955.87, -899.4) * mm, "mid": v(-961.86, -884.93) * mm, "end": v(-976.33, -878.94) * mm});
            skLineSegment(sketch, "E590", {"start": v(-919.9, -1156.05) * mm, "end": v(-792.93, -1156.05) * mm});
            skLineSegment(sketch, "E591", {"start": v(-792.93, -1181.2) * mm, "end": v(-792.93, -1156.05) * mm});
            skLineSegment(sketch, "E592", {"start": v(-919.9, -878.94) * mm, "end": v(-792.93, -878.94) * mm});
            skLineSegment(sketch, "E593", {"start": v(-792.93, -853.8) * mm, "end": v(-792.93, -878.94) * mm});
            skLineSegment(sketch, "E594", {"start": v(-967.02, -1200.1) * mm, "end": v(-929.22, -1162.3) * mm});
            skLineSegment(sketch, "E595", {"start": v(-967.02, -1162.3) * mm, "end": v(-929.22, -1200.1) * mm});
            skLineSegment(sketch, "E596", {"start": v(-415.74, -1155.8) * mm, "end": v(-724.6, -1155.8) * mm});
            skLineSegment(sketch, "E597", {"start": v(-724.6, -1181.2) * mm, "end": v(-415.74, -1181.2) * mm});
            skLineSegment(sketch, "E598", {"start": v(-724.6, -1155.8) * mm, "end": v(-724.6, -1181.2) * mm});
            skLineSegment(sketch, "E599", {"start": v(-415.74, -1181.2) * mm, "end": v(-415.74, -1155.8) * mm});
            skLineSegment(sketch, "E600", {"start": v(-577.91, -1181.2) * mm, "end": v(-577.91, -1155.8) * mm});
            skLineSegment(sketch, "E601", {"start": v(-562.42, -1181.2) * mm, "end": v(-562.42, -1155.8) * mm});
            skLineSegment(sketch, "E602", {"start": v(-589.07, -1200.1) * mm, "end": v(-551.27, -1162.3) * mm});
            skLineSegment(sketch, "E603", {"start": v(-589.07, -1162.3) * mm, "end": v(-551.27, -1200.1) * mm});
            skLineSegment(sketch, "E604", {"start": v(-204.92, -1156.05) * mm, "end": v(-179.52, -1156.05) * mm});
            skLineSegment(sketch, "E605", {"start": v(-179.52, -853.8) * mm, "end": v(-204.92, -853.8) * mm});
            skLineSegment(sketch, "E606", {"start": v(-204.92, -878.94) * mm, "end": v(-179.52, -878.94) * mm});
            skLineSegment(sketch, "E607", {"start": v(-204.92, -1181.2) * mm, "end": v(-179.52, -1181.2) * mm});
            skLineSegment(sketch, "E608", {"start": v(-204.92, -853.8) * mm, "end": v(-204.92, -1181.2) * mm});
            skLineSegment(sketch, "E609", {"start": v(-179.52, -1181.2) * mm, "end": v(-179.52, -853.8) * mm});
            skLineSegment(sketch, "E610", {"start": v(-223.81, -1200.1) * mm, "end": v(-186.02, -1162.3) * mm});
            skLineSegment(sketch, "E611", {"start": v(-223.81, -1162.3) * mm, "end": v(-186.02, -1200.1) * mm});
            skLineSegment(sketch, "E612", {"start": v(29.27, -1181.2) * mm, "end": v(342.2, -1181.2) * mm});
            skLineSegment(sketch, "E613", {"start": v(29.27, -847.95) * mm, "end": v(342.2, -847.95) * mm});
            skArc(sketch, "E614", {"start": v(194.75, -1132.3) * mm, "mid": v(200.85, -1147.03) * mm, "end": v(215.58, -1153.13) * mm});
            skArc(sketch, "E615", {"start": v(215.58, -876.02) * mm, "mid": v(200.85, -882.12) * mm, "end": v(194.75, -896.84) * mm});
            skLineSegment(sketch, "E616", {"start": v(176.72, -1132.3) * mm, "end": v(176.72, -896.84) * mm});
            skLineSegment(sketch, "E617", {"start": v(194.75, -1132.3) * mm, "end": v(194.75, -896.84) * mm});
            skLineSegment(sketch, "E618", {"start": v(29.27, -1153.13) * mm, "end": v(155.9, -1153.13) * mm});
            skLineSegment(sketch, "E619", {"start": v(29.27, -1181.2) * mm, "end": v(29.27, -1153.13) * mm});
            skArc(sketch, "E620", {"start": v(155.9, -1153.13) * mm, "mid": v(170.62, -1147.03) * mm, "end": v(176.72, -1132.3) * mm});
            skLineSegment(sketch, "E621", {"start": v(29.27, -876.02) * mm, "end": v(155.9, -876.02) * mm});
            skLineSegment(sketch, "E622", {"start": v(29.27, -847.95) * mm, "end": v(29.27, -876.02) * mm});
            skArc(sketch, "E623", {"start": v(176.72, -896.84) * mm, "mid": v(170.62, -882.12) * mm, "end": v(155.9, -876.02) * mm});
            skLineSegment(sketch, "E624", {"start": v(215.58, -1153.13) * mm, "end": v(342.2, -1153.13) * mm});
            skLineSegment(sketch, "E625", {"start": v(342.2, -1181.2) * mm, "end": v(342.2, -1153.13) * mm});
            skLineSegment(sketch, "E626", {"start": v(215.58, -876.02) * mm, "end": v(342.2, -876.02) * mm});
            skLineSegment(sketch, "E627", {"start": v(342.2, -847.95) * mm, "end": v(342.2, -876.02) * mm});
            skLineSegment(sketch, "E628", {"start": v(166.84, -1200.1) * mm, "end": v(204.63, -1162.3) * mm});
            skLineSegment(sketch, "E629", {"start": v(166.84, -1162.3) * mm, "end": v(204.63, -1200.1) * mm});
            skLineSegment(sketch, "E630", {"start": v(720.15, -1181.2) * mm, "end": v(720.15, -1155.8) * mm});
            skLineSegment(sketch, "E631", {"start": v(572.7, -1181.2) * mm, "end": v(572.7, -1155.8) * mm});
            skLineSegment(sketch, "E632", {"start": v(554.67, -1181.2) * mm, "end": v(554.67, -1155.8) * mm});
            skLineSegment(sketch, "E633", {"start": v(407.22, -1155.8) * mm, "end": v(407.22, -1181.2) * mm});
            skLineSegment(sketch, "E634", {"start": v(407.22, -1181.2) * mm, "end": v(720.15, -1181.2) * mm});
            skLineSegment(sketch, "E635", {"start": v(720.15, -1155.8) * mm, "end": v(407.22, -1155.8) * mm});
            skLineSegment(sketch, "E636", {"start": v(544.8, -1200.1) * mm, "end": v(582.59, -1162.3) * mm});
            skLineSegment(sketch, "E637", {"start": v(544.8, -1162.3) * mm, "end": v(582.59, -1200.1) * mm});
            skLineSegment(sketch, "E638", {"start": v(928.94, -876.02) * mm, "end": v(954.34, -876.02) * mm});
            skLineSegment(sketch, "E639", {"start": v(954.34, -847.95) * mm, "end": v(928.94, -847.95) * mm});
            skLineSegment(sketch, "E640", {"start": v(928.94, -1153.13) * mm, "end": v(954.34, -1153.13) * mm});
            skLineSegment(sketch, "E641", {"start": v(928.94, -1181.2) * mm, "end": v(954.34, -1181.2) * mm});
            skLineSegment(sketch, "E642", {"start": v(928.94, -847.95) * mm, "end": v(928.94, -1181.2) * mm});
            skLineSegment(sketch, "E643", {"start": v(954.34, -1181.2) * mm, "end": v(954.34, -847.95) * mm});
            skLineSegment(sketch, "E644", {"start": v(910.04, -1200.1) * mm, "end": v(947.84, -1162.3) * mm});
            skLineSegment(sketch, "E645", {"start": v(910.04, -1162.3) * mm, "end": v(947.84, -1200.1) * mm});
            skLineSegment(sketch, "E646", {"start": v(1162.11, -1181.2) * mm, "end": v(1477.07, -1181.2) * mm});
            skLineSegment(sketch, "E647", {"start": v(1162.11, -840.58) * mm, "end": v(1477.07, -840.58) * mm});
            skArc(sketch, "E648", {"start": v(1329.63, -1128.16) * mm, "mid": v(1335.86, -1143.21) * mm, "end": v(1350.91, -1149.45) * mm});
            skArc(sketch, "E649", {"start": v(1350.91, -872.33) * mm, "mid": v(1335.86, -878.57) * mm, "end": v(1329.63, -893.62) * mm});
            skLineSegment(sketch, "E650", {"start": v(1309.56, -1128.16) * mm, "end": v(1309.56, -893.62) * mm});
            skLineSegment(sketch, "E651", {"start": v(1329.63, -1128.16) * mm, "end": v(1329.63, -893.62) * mm});
            skLineSegment(sketch, "E652", {"start": v(1162.11, -1149.45) * mm, "end": v(1288.27, -1149.45) * mm});
            skLineSegment(sketch, "E653", {"start": v(1162.11, -1181.2) * mm, "end": v(1162.11, -1149.45) * mm});
            skArc(sketch, "E654", {"start": v(1288.27, -1149.45) * mm, "mid": v(1303.32, -1143.21) * mm, "end": v(1309.56, -1128.16) * mm});
            skLineSegment(sketch, "E655", {"start": v(1162.11, -872.33) * mm, "end": v(1288.27, -872.33) * mm});
            skLineSegment(sketch, "E656", {"start": v(1162.11, -840.58) * mm, "end": v(1162.11, -872.33) * mm});
            skArc(sketch, "E657", {"start": v(1309.56, -893.62) * mm, "mid": v(1303.32, -878.57) * mm, "end": v(1288.27, -872.33) * mm});
            skLineSegment(sketch, "E658", {"start": v(1350.91, -1149.45) * mm, "end": v(1477.07, -1149.45) * mm});
            skLineSegment(sketch, "E659", {"start": v(1477.07, -1181.2) * mm, "end": v(1477.07, -1149.45) * mm});
            skLineSegment(sketch, "E660", {"start": v(1350.91, -872.33) * mm, "end": v(1477.07, -872.33) * mm});
            skLineSegment(sketch, "E661", {"start": v(1477.07, -840.58) * mm, "end": v(1477.07, -872.33) * mm});
            skLineSegment(sketch, "E662", {"start": v(1300.7, -1200.1) * mm, "end": v(1338.5, -1162.3) * mm});
            skLineSegment(sketch, "E663", {"start": v(1300.7, -1162.3) * mm, "end": v(1338.5, -1200.1) * mm});
            skLineSegment(sketch, "E664", {"start": v(1541.08, -1155.8) * mm, "end": v(1541.08, -1181.2) * mm});
            skLineSegment(sketch, "E665", {"start": v(1687.51, -1181.2) * mm, "end": v(1687.51, -1155.8) * mm});
            skLineSegment(sketch, "E666", {"start": v(1707.58, -1181.2) * mm, "end": v(1707.58, -1155.8) * mm});
            skLineSegment(sketch, "E667", {"start": v(1854, -1181.2) * mm, "end": v(1854, -1155.8) * mm});
            skLineSegment(sketch, "E668", {"start": v(1541.08, -1181.2) * mm, "end": v(1854, -1181.2) * mm});
            skLineSegment(sketch, "E669", {"start": v(1854, -1155.8) * mm, "end": v(1541.08, -1155.8) * mm});
            skLineSegment(sketch, "E670", {"start": v(1678.65, -1200.1) * mm, "end": v(1716.44, -1162.3) * mm});
            skLineSegment(sketch, "E671", {"start": v(1678.65, -1162.3) * mm, "end": v(1716.44, -1200.1) * mm});
            skLineSegment(sketch, "E672", {"start": v(2088.2, -840.58) * mm, "end": v(2062.8, -840.58) * mm});
            skLineSegment(sketch, "E673", {"start": v(2062.8, -872.33) * mm, "end": v(2088.2, -872.33) * mm});
            skLineSegment(sketch, "E674", {"start": v(2062.8, -1181.2) * mm, "end": v(2088.2, -1181.2) * mm});
            skLineSegment(sketch, "E675", {"start": v(2062.8, -1149.45) * mm, "end": v(2088.2, -1149.45) * mm});
            skLineSegment(sketch, "E676", {"start": v(2062.8, -840.58) * mm, "end": v(2062.8, -1181.2) * mm});
            skLineSegment(sketch, "E677", {"start": v(2088.2, -1181.2) * mm, "end": v(2088.2, -840.58) * mm});
            skLineSegment(sketch, "E678", {"start": v(2043.9, -1200.1) * mm, "end": v(2081.7, -1162.3) * mm});
            skLineSegment(sketch, "E679", {"start": v(2043.9, -1162.3) * mm, "end": v(2081.7, -1200.1) * mm});
            skSolve(sketch);
        }
        {
            var Q0;
            Q0 = qSketchRegion(id + "F0", true);
            extrude(context, id + "F1", {"entities" : qUnion([Q0]), "depth" : 609.6 * mm});
        }
        {
            var Q0;
            Q0=makeQuery(id+"F1.opExtrude","SWEPT_BODY",BODY,{"disambiguationData":[OSD([sQuery(id+"F0.wireOp",EDGE,"E154"),sQuery(id+"F0.wireOp",EDGE,"E157"),sQuery(id+"F0.wireOp",EDGE,"E158"),sQuery(id+"F0.wireOp",EDGE,"E159")])]});
            var Q1;
            Q1=makeQuery(id+"F1.opExtrude","SWEPT_BODY",BODY,{"disambiguationData":[OSD([sQuery(id+"F0.wireOp",EDGE,"E162"),sQuery(id+"F0.wireOp",EDGE,"E163"),sQuery(id+"F0.wireOp",EDGE,"E166"),sQuery(id+"F0.wireOp",EDGE,"E167")])]});
            var Q2;
            Q2=makeQuery(id+"F1.opExtrude","SWEPT_BODY",BODY,{"disambiguationData":[OSD([sQuery(id+"F0.wireOp",EDGE,"E170"),sQuery(id+"F0.wireOp",EDGE,"E171"),sQuery(id+"F0.wireOp",EDGE,"E172"),sQuery(id+"F0.wireOp",EDGE,"E173"),sQuery(id+"F0.wireOp",EDGE,"E174"),sQuery(id+"F0.wireOp",EDGE,"E175"),sQuery(id+"F0.wireOp",EDGE,"E176"),sQuery(id+"F0.wireOp",EDGE,"E177"),sQuery(id+"F0.wireOp",EDGE,"E178"),sQuery(id+"F0.wireOp",EDGE,"E179"),sQuery(id+"F0.wireOp",EDGE,"E180"),sQuery(id+"F0.wireOp",EDGE,"E181"),sQuery(id+"F0.wireOp",EDGE,"E182"),sQuery(id+"F0.wireOp",EDGE,"E183"),sQuery(id+"F0.wireOp",EDGE,"E184"),sQuery(id+"F0.wireOp",EDGE,"E185")])]});
            var Q3;
            Q3=makeQuery(id+"F1.opExtrude","SWEPT_BODY",BODY,{"disambiguationData":[OSD([sQuery(id+"F0.wireOp",EDGE,"E188"),sQuery(id+"F0.wireOp",EDGE,"E191"),sQuery(id+"F0.wireOp",EDGE,"E192"),sQuery(id+"F0.wireOp",EDGE,"E193")])]});
            var Q4;
            Q4=makeQuery(id+"F1.opExtrude","SWEPT_BODY",BODY,{"disambiguationData":[OSD([sQuery(id+"F0.wireOp",EDGE,"E196"),sQuery(id+"F0.wireOp",EDGE,"E198"),sQuery(id+"F0.wireOp",EDGE,"E200"),sQuery(id+"F0.wireOp",EDGE,"E201")])]});
            var Q5;
            Q5=makeQuery(id+"F1.opExtrude","SWEPT_BODY",BODY,{"disambiguationData":[OSD([sQuery(id+"F0.wireOp",EDGE,"E204"),sQuery(id+"F0.wireOp",EDGE,"E205"),sQuery(id+"F0.wireOp",EDGE,"E206"),sQuery(id+"F0.wireOp",EDGE,"E207"),sQuery(id+"F0.wireOp",EDGE,"E208"),sQuery(id+"F0.wireOp",EDGE,"E209"),sQuery(id+"F0.wireOp",EDGE,"E210"),sQuery(id+"F0.wireOp",EDGE,"E211"),sQuery(id+"F0.wireOp",EDGE,"E212"),sQuery(id+"F0.wireOp",EDGE,"E213"),sQuery(id+"F0.wireOp",EDGE,"E214"),sQuery(id+"F0.wireOp",EDGE,"E215"),sQuery(id+"F0.wireOp",EDGE,"E216"),sQuery(id+"F0.wireOp",EDGE,"E217"),sQuery(id+"F0.wireOp",EDGE,"E218"),sQuery(id+"F0.wireOp",EDGE,"E219")])]});
            var Q6;
            Q6=makeQuery(id+"F1.opExtrude","SWEPT_BODY",BODY,{"disambiguationData":[OSD([sQuery(id+"F0.wireOp",EDGE,"E222"),sQuery(id+"F0.wireOp",EDGE,"E223"),sQuery(id+"F0.wireOp",EDGE,"E226"),sQuery(id+"F0.wireOp",EDGE,"E227")])]});
            var Q7;
            Q7=makeQuery(id+"F1.opExtrude","SWEPT_BODY",BODY,{"disambiguationData":[OSD([sQuery(id+"F0.wireOp",EDGE,"E230"),sQuery(id+"F0.wireOp",EDGE,"E231"),sQuery(id+"F0.wireOp",EDGE,"E234"),sQuery(id+"F0.wireOp",EDGE,"E235")])]});
            var Q8;
            Q8=makeQuery(id+"F1.opExtrude","SWEPT_BODY",BODY,{"disambiguationData":[OSD([sQuery(id+"F0.wireOp",EDGE,"E238"),sQuery(id+"F0.wireOp",EDGE,"E239"),sQuery(id+"F0.wireOp",EDGE,"E240"),sQuery(id+"F0.wireOp",EDGE,"E241"),sQuery(id+"F0.wireOp",EDGE,"E242"),sQuery(id+"F0.wireOp",EDGE,"E243"),sQuery(id+"F0.wireOp",EDGE,"E244"),sQuery(id+"F0.wireOp",EDGE,"E245"),sQuery(id+"F0.wireOp",EDGE,"E246"),sQuery(id+"F0.wireOp",EDGE,"E247"),sQuery(id+"F0.wireOp",EDGE,"E248"),sQuery(id+"F0.wireOp",EDGE,"E249"),sQuery(id+"F0.wireOp",EDGE,"E250"),sQuery(id+"F0.wireOp",EDGE,"E251"),sQuery(id+"F0.wireOp",EDGE,"E252"),sQuery(id+"F0.wireOp",EDGE,"E253")])]});
            var Q9;
            Q9=makeQuery(id+"F1.opExtrude","SWEPT_BODY",BODY,{"disambiguationData":[OSD([sQuery(id+"F0.wireOp",EDGE,"E256"),sQuery(id+"F0.wireOp",EDGE,"E257"),sQuery(id+"F0.wireOp",EDGE,"E260"),sQuery(id+"F0.wireOp",EDGE,"E261")])]});
            var Q10;
            Q10=makeQuery(id+"F1.opExtrude","SWEPT_BODY",BODY,{"disambiguationData":[OSD([sQuery(id+"F0.wireOp",EDGE,"E264"),sQuery(id+"F0.wireOp",EDGE,"E266"),sQuery(id+"F0.wireOp",EDGE,"E268"),sQuery(id+"F0.wireOp",EDGE,"E269")])]});
            var Q11;
            Q11=makeQuery(id+"F1.opExtrude","SWEPT_BODY",BODY,{"disambiguationData":[OSD([sQuery(id+"F0.wireOp",EDGE,"E272"),sQuery(id+"F0.wireOp",EDGE,"E273"),sQuery(id+"F0.wireOp",EDGE,"E274"),sQuery(id+"F0.wireOp",EDGE,"E275"),sQuery(id+"F0.wireOp",EDGE,"E276"),sQuery(id+"F0.wireOp",EDGE,"E277"),sQuery(id+"F0.wireOp",EDGE,"E278"),sQuery(id+"F0.wireOp",EDGE,"E279"),sQuery(id+"F0.wireOp",EDGE,"E280"),sQuery(id+"F0.wireOp",EDGE,"E281"),sQuery(id+"F0.wireOp",EDGE,"E282"),sQuery(id+"F0.wireOp",EDGE,"E283"),sQuery(id+"F0.wireOp",EDGE,"E284"),sQuery(id+"F0.wireOp",EDGE,"E285"),sQuery(id+"F0.wireOp",EDGE,"E286"),sQuery(id+"F0.wireOp",EDGE,"E287")])]});
            var Q12;
            Q12=makeQuery(id+"F1.opExtrude","SWEPT_BODY",BODY,{"disambiguationData":[OSD([sQuery(id+"F0.wireOp",EDGE,"E290"),sQuery(id+"F0.wireOp",EDGE,"E291"),sQuery(id+"F0.wireOp",EDGE,"E292"),sQuery(id+"F0.wireOp",EDGE,"E295")])]});
            var Q13;
            Q13=makeQuery(id+"F1.opExtrude","SWEPT_BODY",BODY,{"disambiguationData":[OSD([sQuery(id+"F0.wireOp",EDGE,"E298"),sQuery(id+"F0.wireOp",EDGE,"E299"),sQuery(id+"F0.wireOp",EDGE,"E300"),sQuery(id+"F0.wireOp",EDGE,"E302")])]});
            var Q14;
            Q14=makeQuery(id+"F1.opExtrude","SWEPT_BODY",BODY,{"disambiguationData":[OSD([sQuery(id+"F0.wireOp",EDGE,"E306"),sQuery(id+"F0.wireOp",EDGE,"E307"),sQuery(id+"F0.wireOp",EDGE,"E308"),sQuery(id+"F0.wireOp",EDGE,"E309"),sQuery(id+"F0.wireOp",EDGE,"E310"),sQuery(id+"F0.wireOp",EDGE,"E311"),sQuery(id+"F0.wireOp",EDGE,"E312"),sQuery(id+"F0.wireOp",EDGE,"E313"),sQuery(id+"F0.wireOp",EDGE,"E314"),sQuery(id+"F0.wireOp",EDGE,"E315"),sQuery(id+"F0.wireOp",EDGE,"E316"),sQuery(id+"F0.wireOp",EDGE,"E317"),sQuery(id+"F0.wireOp",EDGE,"E318"),sQuery(id+"F0.wireOp",EDGE,"E319"),sQuery(id+"F0.wireOp",EDGE,"E320"),sQuery(id+"F0.wireOp",EDGE,"E321")])]});
            var Q15;
            Q15=makeQuery(id+"F1.opExtrude","SWEPT_BODY",BODY,{"disambiguationData":[OSD([sQuery(id+"F0.wireOp",EDGE,"E324"),sQuery(id+"F0.wireOp",EDGE,"E325"),sQuery(id+"F0.wireOp",EDGE,"E328"),sQuery(id+"F0.wireOp",EDGE,"E329")])]});
            var Q16;
            Q16=makeQuery(id+"F1.opExtrude","SWEPT_BODY",BODY,{"disambiguationData":[OSD([sQuery(id+"F0.wireOp",EDGE,"E333"),sQuery(id+"F0.wireOp",EDGE,"E335"),sQuery(id+"F0.wireOp",EDGE,"E336"),sQuery(id+"F0.wireOp",EDGE,"E337")])]});
            var Q17;
            Q17=makeQuery(id+"F1.opExtrude","SWEPT_BODY",BODY,{"disambiguationData":[OSD([sQuery(id+"F0.wireOp",EDGE,"E340"),sQuery(id+"F0.wireOp",EDGE,"E341"),sQuery(id+"F0.wireOp",EDGE,"E342"),sQuery(id+"F0.wireOp",EDGE,"E343"),sQuery(id+"F0.wireOp",EDGE,"E344"),sQuery(id+"F0.wireOp",EDGE,"E345"),sQuery(id+"F0.wireOp",EDGE,"E346"),sQuery(id+"F0.wireOp",EDGE,"E347"),sQuery(id+"F0.wireOp",EDGE,"E348"),sQuery(id+"F0.wireOp",EDGE,"E349"),sQuery(id+"F0.wireOp",EDGE,"E350"),sQuery(id+"F0.wireOp",EDGE,"E351"),sQuery(id+"F0.wireOp",EDGE,"E352"),sQuery(id+"F0.wireOp",EDGE,"E353"),sQuery(id+"F0.wireOp",EDGE,"E354"),sQuery(id+"F0.wireOp",EDGE,"E355")])]});
            var Q18;
            Q18=makeQuery(id+"F1.opExtrude","SWEPT_BODY",BODY,{"disambiguationData":[OSD([sQuery(id+"F0.wireOp",EDGE,"E358"),sQuery(id+"F0.wireOp",EDGE,"E361"),sQuery(id+"F0.wireOp",EDGE,"E362"),sQuery(id+"F0.wireOp",EDGE,"E363")])]});
            var Q19;
            Q19=makeQuery(id+"F1.opExtrude","SWEPT_BODY",BODY,{"disambiguationData":[OSD([sQuery(id+"F0.wireOp",EDGE,"E366"),sQuery(id+"F0.wireOp",EDGE,"E368"),sQuery(id+"F0.wireOp",EDGE,"E370"),sQuery(id+"F0.wireOp",EDGE,"E371")])]});
            var Q20;
            Q20=makeQuery(id+"F1.opExtrude","SWEPT_BODY",BODY,{"disambiguationData":[OSD([sQuery(id+"F0.wireOp",EDGE,"E374"),sQuery(id+"F0.wireOp",EDGE,"E375"),sQuery(id+"F0.wireOp",EDGE,"E376"),sQuery(id+"F0.wireOp",EDGE,"E377"),sQuery(id+"F0.wireOp",EDGE,"E378"),sQuery(id+"F0.wireOp",EDGE,"E379"),sQuery(id+"F0.wireOp",EDGE,"E380"),sQuery(id+"F0.wireOp",EDGE,"E381"),sQuery(id+"F0.wireOp",EDGE,"E382"),sQuery(id+"F0.wireOp",EDGE,"E383"),sQuery(id+"F0.wireOp",EDGE,"E384"),sQuery(id+"F0.wireOp",EDGE,"E385"),sQuery(id+"F0.wireOp",EDGE,"E386"),sQuery(id+"F0.wireOp",EDGE,"E387"),sQuery(id+"F0.wireOp",EDGE,"E388"),sQuery(id+"F0.wireOp",EDGE,"E389")])]});
            var Q21;
            Q21=makeQuery(id+"F1.opExtrude","SWEPT_BODY",BODY,{"disambiguationData":[OSD([sQuery(id+"F0.wireOp",EDGE,"E392"),sQuery(id+"F0.wireOp",EDGE,"E393"),sQuery(id+"F0.wireOp",EDGE,"E396"),sQuery(id+"F0.wireOp",EDGE,"E397")])]});
            var Q22;
            Q22=makeQuery(id+"F1.opExtrude","SWEPT_BODY",BODY,{"disambiguationData":[OSD([sQuery(id+"F0.wireOp",EDGE,"E400"),sQuery(id+"F0.wireOp",EDGE,"E401"),sQuery(id+"F0.wireOp",EDGE,"E402"),sQuery(id+"F0.wireOp",EDGE,"E404")])]});
            var Q23;
            Q23=makeQuery(id+"F1.opExtrude","SWEPT_BODY",BODY,{"disambiguationData":[OSD([sQuery(id+"F0.wireOp",EDGE,"E408"),sQuery(id+"F0.wireOp",EDGE,"E409"),sQuery(id+"F0.wireOp",EDGE,"E410"),sQuery(id+"F0.wireOp",EDGE,"E411"),sQuery(id+"F0.wireOp",EDGE,"E412"),sQuery(id+"F0.wireOp",EDGE,"E413"),sQuery(id+"F0.wireOp",EDGE,"E414"),sQuery(id+"F0.wireOp",EDGE,"E415"),sQuery(id+"F0.wireOp",EDGE,"E416"),sQuery(id+"F0.wireOp",EDGE,"E417"),sQuery(id+"F0.wireOp",EDGE,"E418"),sQuery(id+"F0.wireOp",EDGE,"E419"),sQuery(id+"F0.wireOp",EDGE,"E420"),sQuery(id+"F0.wireOp",EDGE,"E421"),sQuery(id+"F0.wireOp",EDGE,"E422"),sQuery(id+"F0.wireOp",EDGE,"E423")])]});
            var Q24;
            Q24=makeQuery(id+"F1.opExtrude","SWEPT_BODY",BODY,{"disambiguationData":[OSD([sQuery(id+"F0.wireOp",EDGE,"E426"),sQuery(id+"F0.wireOp",EDGE,"E429"),sQuery(id+"F0.wireOp",EDGE,"E430"),sQuery(id+"F0.wireOp",EDGE,"E431")])]});
            var Q25;
            Q25=makeQuery(id+"F1.opExtrude","SWEPT_BODY",BODY,{"disambiguationData":[OSD([sQuery(id+"F0.wireOp",EDGE,"E434"),sQuery(id+"F0.wireOp",EDGE,"E435"),sQuery(id+"F0.wireOp",EDGE,"E436"),sQuery(id+"F0.wireOp",EDGE,"E438")])]});
            var Q26;
            Q26=makeQuery(id+"F1.opExtrude","SWEPT_BODY",BODY,{"disambiguationData":[OSD([sQuery(id+"F0.wireOp",EDGE,"E442"),sQuery(id+"F0.wireOp",EDGE,"E443"),sQuery(id+"F0.wireOp",EDGE,"E444"),sQuery(id+"F0.wireOp",EDGE,"E445"),sQuery(id+"F0.wireOp",EDGE,"E446"),sQuery(id+"F0.wireOp",EDGE,"E447"),sQuery(id+"F0.wireOp",EDGE,"E448"),sQuery(id+"F0.wireOp",EDGE,"E449"),sQuery(id+"F0.wireOp",EDGE,"E450"),sQuery(id+"F0.wireOp",EDGE,"E451"),sQuery(id+"F0.wireOp",EDGE,"E452"),sQuery(id+"F0.wireOp",EDGE,"E453"),sQuery(id+"F0.wireOp",EDGE,"E454"),sQuery(id+"F0.wireOp",EDGE,"E455"),sQuery(id+"F0.wireOp",EDGE,"E456"),sQuery(id+"F0.wireOp",EDGE,"E457")])]});
            var Q27;
            Q27=makeQuery(id+"F1.opExtrude","SWEPT_BODY",BODY,{"disambiguationData":[OSD([sQuery(id+"F0.wireOp",EDGE,"E460"),sQuery(id+"F0.wireOp",EDGE,"E463"),sQuery(id+"F0.wireOp",EDGE,"E464"),sQuery(id+"F0.wireOp",EDGE,"E465")])]});
            var Q28;
            Q28=makeQuery(id+"F1.opExtrude","SWEPT_BODY",BODY,{"disambiguationData":[OSD([sQuery(id+"F0.wireOp",EDGE,"E468"),sQuery(id+"F0.wireOp",EDGE,"E469"),sQuery(id+"F0.wireOp",EDGE,"E470"),sQuery(id+"F0.wireOp",EDGE,"E472")])]});
            var Q29;
            Q29=makeQuery(id+"F1.opExtrude","SWEPT_BODY",BODY,{"disambiguationData":[OSD([sQuery(id+"F0.wireOp",EDGE,"E476"),sQuery(id+"F0.wireOp",EDGE,"E477"),sQuery(id+"F0.wireOp",EDGE,"E478"),sQuery(id+"F0.wireOp",EDGE,"E479"),sQuery(id+"F0.wireOp",EDGE,"E480"),sQuery(id+"F0.wireOp",EDGE,"E481"),sQuery(id+"F0.wireOp",EDGE,"E482"),sQuery(id+"F0.wireOp",EDGE,"E483"),sQuery(id+"F0.wireOp",EDGE,"E484"),sQuery(id+"F0.wireOp",EDGE,"E485"),sQuery(id+"F0.wireOp",EDGE,"E486"),sQuery(id+"F0.wireOp",EDGE,"E487"),sQuery(id+"F0.wireOp",EDGE,"E488"),sQuery(id+"F0.wireOp",EDGE,"E489"),sQuery(id+"F0.wireOp",EDGE,"E490"),sQuery(id+"F0.wireOp",EDGE,"E491")])]});
            var Q30;
            Q30=makeQuery(id+"F1.opExtrude","SWEPT_BODY",BODY,{"disambiguationData":[OSD([sQuery(id+"F0.wireOp",EDGE,"E494"),sQuery(id+"F0.wireOp",EDGE,"E495"),sQuery(id+"F0.wireOp",EDGE,"E496"),sQuery(id+"F0.wireOp",EDGE,"E497")])]});
            var Q31;
            Q31=makeQuery(id+"F1.opExtrude","SWEPT_BODY",BODY,{"disambiguationData":[OSD([sQuery(id+"F0.wireOp",EDGE,"E502"),sQuery(id+"F0.wireOp",EDGE,"E504"),sQuery(id+"F0.wireOp",EDGE,"E506"),sQuery(id+"F0.wireOp",EDGE,"E507")])]});
            var Q32;
            Q32=makeQuery(id+"F1.opExtrude","SWEPT_BODY",BODY,{"disambiguationData":[OSD([sQuery(id+"F0.wireOp",EDGE,"E510"),sQuery(id+"F0.wireOp",EDGE,"E511"),sQuery(id+"F0.wireOp",EDGE,"E512"),sQuery(id+"F0.wireOp",EDGE,"E513"),sQuery(id+"F0.wireOp",EDGE,"E514"),sQuery(id+"F0.wireOp",EDGE,"E515"),sQuery(id+"F0.wireOp",EDGE,"E516"),sQuery(id+"F0.wireOp",EDGE,"E517"),sQuery(id+"F0.wireOp",EDGE,"E518"),sQuery(id+"F0.wireOp",EDGE,"E519"),sQuery(id+"F0.wireOp",EDGE,"E520"),sQuery(id+"F0.wireOp",EDGE,"E521"),sQuery(id+"F0.wireOp",EDGE,"E522"),sQuery(id+"F0.wireOp",EDGE,"E523"),sQuery(id+"F0.wireOp",EDGE,"E524"),sQuery(id+"F0.wireOp",EDGE,"E525")])]});
            var Q33;
            Q33=makeQuery(id+"F1.opExtrude","SWEPT_BODY",BODY,{"disambiguationData":[OSD([sQuery(id+"F0.wireOp",EDGE,"E528"),sQuery(id+"F0.wireOp",EDGE,"E531"),sQuery(id+"F0.wireOp",EDGE,"E532"),sQuery(id+"F0.wireOp",EDGE,"E533")])]});
            var Q34;
            Q34=makeQuery(id+"F1.opExtrude","SWEPT_BODY",BODY,{"disambiguationData":[OSD([sQuery(id+"F0.wireOp",EDGE,"E536"),sQuery(id+"F0.wireOp",EDGE,"E538"),sQuery(id+"F0.wireOp",EDGE,"E540"),sQuery(id+"F0.wireOp",EDGE,"E541")])]});
            var Q35;
            Q35=makeQuery(id+"F1.opExtrude","SWEPT_BODY",BODY,{"disambiguationData":[OSD([sQuery(id+"F0.wireOp",EDGE,"E544"),sQuery(id+"F0.wireOp",EDGE,"E545"),sQuery(id+"F0.wireOp",EDGE,"E546"),sQuery(id+"F0.wireOp",EDGE,"E547"),sQuery(id+"F0.wireOp",EDGE,"E548"),sQuery(id+"F0.wireOp",EDGE,"E549"),sQuery(id+"F0.wireOp",EDGE,"E550"),sQuery(id+"F0.wireOp",EDGE,"E551"),sQuery(id+"F0.wireOp",EDGE,"E552"),sQuery(id+"F0.wireOp",EDGE,"E553"),sQuery(id+"F0.wireOp",EDGE,"E554"),sQuery(id+"F0.wireOp",EDGE,"E555"),sQuery(id+"F0.wireOp",EDGE,"E556"),sQuery(id+"F0.wireOp",EDGE,"E557"),sQuery(id+"F0.wireOp",EDGE,"E558"),sQuery(id+"F0.wireOp",EDGE,"E559")])]});
            var Q36;
            Q36=makeQuery(id+"F1.opExtrude","SWEPT_BODY",BODY,{"disambiguationData":[OSD([sQuery(id+"F0.wireOp",EDGE,"E562"),sQuery(id+"F0.wireOp",EDGE,"E565"),sQuery(id+"F0.wireOp",EDGE,"E566"),sQuery(id+"F0.wireOp",EDGE,"E567")])]});
            var Q37;
            Q37=makeQuery(id+"F1.opExtrude","SWEPT_BODY",BODY,{"disambiguationData":[OSD([sQuery(id+"F0.wireOp",EDGE,"E570"),sQuery(id+"F0.wireOp",EDGE,"E571"),sQuery(id+"F0.wireOp",EDGE,"E572"),sQuery(id+"F0.wireOp",EDGE,"E574")])]});
            var Q38;
            Q38=makeQuery(id+"F1.opExtrude","SWEPT_BODY",BODY,{"disambiguationData":[OSD([sQuery(id+"F0.wireOp",EDGE,"E578"),sQuery(id+"F0.wireOp",EDGE,"E579"),sQuery(id+"F0.wireOp",EDGE,"E580"),sQuery(id+"F0.wireOp",EDGE,"E581"),sQuery(id+"F0.wireOp",EDGE,"E582"),sQuery(id+"F0.wireOp",EDGE,"E583"),sQuery(id+"F0.wireOp",EDGE,"E584"),sQuery(id+"F0.wireOp",EDGE,"E585"),sQuery(id+"F0.wireOp",EDGE,"E586"),sQuery(id+"F0.wireOp",EDGE,"E587"),sQuery(id+"F0.wireOp",EDGE,"E588"),sQuery(id+"F0.wireOp",EDGE,"E589"),sQuery(id+"F0.wireOp",EDGE,"E590"),sQuery(id+"F0.wireOp",EDGE,"E591"),sQuery(id+"F0.wireOp",EDGE,"E592"),sQuery(id+"F0.wireOp",EDGE,"E593")])]});
            var Q39;
            Q39=makeQuery(id+"F1.opExtrude","SWEPT_BODY",BODY,{"disambiguationData":[OSD([sQuery(id+"F0.wireOp",EDGE,"E596"),sQuery(id+"F0.wireOp",EDGE,"E597"),sQuery(id+"F0.wireOp",EDGE,"E598"),sQuery(id+"F0.wireOp",EDGE,"E599")])]});
            var Q40;
            Q40=makeQuery(id+"F1.opExtrude","SWEPT_BODY",BODY,{"disambiguationData":[OSD([sQuery(id+"F0.wireOp",EDGE,"E605"),sQuery(id+"F0.wireOp",EDGE,"E607"),sQuery(id+"F0.wireOp",EDGE,"E608"),sQuery(id+"F0.wireOp",EDGE,"E609")])]});
            var Q41;
            Q41=makeQuery(id+"F1.opExtrude","SWEPT_BODY",BODY,{"disambiguationData":[OSD([sQuery(id+"F0.wireOp",EDGE,"E612"),sQuery(id+"F0.wireOp",EDGE,"E613"),sQuery(id+"F0.wireOp",EDGE,"E614"),sQuery(id+"F0.wireOp",EDGE,"E615"),sQuery(id+"F0.wireOp",EDGE,"E616"),sQuery(id+"F0.wireOp",EDGE,"E617"),sQuery(id+"F0.wireOp",EDGE,"E618"),sQuery(id+"F0.wireOp",EDGE,"E619"),sQuery(id+"F0.wireOp",EDGE,"E620"),sQuery(id+"F0.wireOp",EDGE,"E621"),sQuery(id+"F0.wireOp",EDGE,"E622"),sQuery(id+"F0.wireOp",EDGE,"E623"),sQuery(id+"F0.wireOp",EDGE,"E624"),sQuery(id+"F0.wireOp",EDGE,"E625"),sQuery(id+"F0.wireOp",EDGE,"E626"),sQuery(id+"F0.wireOp",EDGE,"E627")])]});
            var Q42;
            Q42=makeQuery(id+"F1.opExtrude","SWEPT_BODY",BODY,{"disambiguationData":[OSD([sQuery(id+"F0.wireOp",EDGE,"E630"),sQuery(id+"F0.wireOp",EDGE,"E633"),sQuery(id+"F0.wireOp",EDGE,"E634"),sQuery(id+"F0.wireOp",EDGE,"E635")])]});
            var Q43;
            Q43=makeQuery(id+"F1.opExtrude","SWEPT_BODY",BODY,{"disambiguationData":[OSD([sQuery(id+"F0.wireOp",EDGE,"E639"),sQuery(id+"F0.wireOp",EDGE,"E641"),sQuery(id+"F0.wireOp",EDGE,"E642"),sQuery(id+"F0.wireOp",EDGE,"E643")])]});
            var Q44;
            Q44=makeQuery(id+"F1.opExtrude","SWEPT_BODY",BODY,{"disambiguationData":[OSD([sQuery(id+"F0.wireOp",EDGE,"E646"),sQuery(id+"F0.wireOp",EDGE,"E647"),sQuery(id+"F0.wireOp",EDGE,"E648"),sQuery(id+"F0.wireOp",EDGE,"E649"),sQuery(id+"F0.wireOp",EDGE,"E650"),sQuery(id+"F0.wireOp",EDGE,"E651"),sQuery(id+"F0.wireOp",EDGE,"E652"),sQuery(id+"F0.wireOp",EDGE,"E653"),sQuery(id+"F0.wireOp",EDGE,"E654"),sQuery(id+"F0.wireOp",EDGE,"E655"),sQuery(id+"F0.wireOp",EDGE,"E656"),sQuery(id+"F0.wireOp",EDGE,"E657"),sQuery(id+"F0.wireOp",EDGE,"E658"),sQuery(id+"F0.wireOp",EDGE,"E659"),sQuery(id+"F0.wireOp",EDGE,"E660"),sQuery(id+"F0.wireOp",EDGE,"E661")])]});
            var Q45;
            Q45=makeQuery(id+"F1.opExtrude","SWEPT_BODY",BODY,{"disambiguationData":[OSD([sQuery(id+"F0.wireOp",EDGE,"E664"),sQuery(id+"F0.wireOp",EDGE,"E667"),sQuery(id+"F0.wireOp",EDGE,"E668"),sQuery(id+"F0.wireOp",EDGE,"E669")])]});
            var Q46;
            Q46=makeQuery(id+"F1.opExtrude","SWEPT_BODY",BODY,{"disambiguationData":[OSD([sQuery(id+"F0.wireOp",EDGE,"E672"),sQuery(id+"F0.wireOp",EDGE,"E674"),sQuery(id+"F0.wireOp",EDGE,"E676"),sQuery(id+"F0.wireOp",EDGE,"E677")])]});
            var Q47;
            Q47=makeQuery(id+"F1.opExtrude","SWEPT_BODY",BODY,{"disambiguationData":[OSD([sQuery(id+"F0.wireOp",EDGE,"E128"),sQuery(id+"F0.wireOp",EDGE,"E130"),sQuery(id+"F0.wireOp",EDGE,"E132"),sQuery(id+"F0.wireOp",EDGE,"E133")])]});
            var Q48;
            Q48=makeQuery(id+"F1.opExtrude","SWEPT_BODY",BODY,{"disambiguationData":[OSD([sQuery(id+"F0.wireOp",EDGE,"E0"),sQuery(id+"F0.wireOp",EDGE,"E1"),sQuery(id+"F0.wireOp",EDGE,"E2"),sQuery(id+"F0.wireOp",EDGE,"E3"),sQuery(id+"F0.wireOp",EDGE,"E4"),sQuery(id+"F0.wireOp",EDGE,"E5"),sQuery(id+"F0.wireOp",EDGE,"E6"),sQuery(id+"F0.wireOp",EDGE,"E7"),sQuery(id+"F0.wireOp",EDGE,"E8"),sQuery(id+"F0.wireOp",EDGE,"E9"),sQuery(id+"F0.wireOp",EDGE,"E10"),sQuery(id+"F0.wireOp",EDGE,"E11"),sQuery(id+"F0.wireOp",EDGE,"E12"),sQuery(id+"F0.wireOp",EDGE,"E13"),sQuery(id+"F0.wireOp",EDGE,"E14"),sQuery(id+"F0.wireOp",EDGE,"E15")])]});
            var Q49;
            Q49=makeQuery(id+"F1.opExtrude","SWEPT_BODY",BODY,{"disambiguationData":[OSD([sQuery(id+"F0.wireOp",EDGE,"E18"),sQuery(id+"F0.wireOp",EDGE,"E19"),sQuery(id+"F0.wireOp",EDGE,"E22"),sQuery(id+"F0.wireOp",EDGE,"E23")])]});
            var Q50;
            Q50=makeQuery(id+"F1.opExtrude","SWEPT_BODY",BODY,{"disambiguationData":[OSD([sQuery(id+"F0.wireOp",EDGE,"E28"),sQuery(id+"F0.wireOp",EDGE,"E29"),sQuery(id+"F0.wireOp",EDGE,"E30"),sQuery(id+"F0.wireOp",EDGE,"E31")])]});
            var Q51;
            Q51=makeQuery(id+"F1.opExtrude","SWEPT_BODY",BODY,{"disambiguationData":[OSD([sQuery(id+"F0.wireOp",EDGE,"E34"),sQuery(id+"F0.wireOp",EDGE,"E35"),sQuery(id+"F0.wireOp",EDGE,"E36"),sQuery(id+"F0.wireOp",EDGE,"E37"),sQuery(id+"F0.wireOp",EDGE,"E38"),sQuery(id+"F0.wireOp",EDGE,"E39"),sQuery(id+"F0.wireOp",EDGE,"E40"),sQuery(id+"F0.wireOp",EDGE,"E41"),sQuery(id+"F0.wireOp",EDGE,"E42"),sQuery(id+"F0.wireOp",EDGE,"E43"),sQuery(id+"F0.wireOp",EDGE,"E44"),sQuery(id+"F0.wireOp",EDGE,"E45"),sQuery(id+"F0.wireOp",EDGE,"E46"),sQuery(id+"F0.wireOp",EDGE,"E47"),sQuery(id+"F0.wireOp",EDGE,"E48"),sQuery(id+"F0.wireOp",EDGE,"E49")])]});
            var Q52;
            Q52=makeQuery(id+"F1.opExtrude","SWEPT_BODY",BODY,{"disambiguationData":[OSD([sQuery(id+"F0.wireOp",EDGE,"E52"),sQuery(id+"F0.wireOp",EDGE,"E53"),sQuery(id+"F0.wireOp",EDGE,"E54"),sQuery(id+"F0.wireOp",EDGE,"E57")])]});
            var Q53;
            Q53=makeQuery(id+"F1.opExtrude","SWEPT_BODY",BODY,{"disambiguationData":[OSD([sQuery(id+"F0.wireOp",EDGE,"E60"),sQuery(id+"F0.wireOp",EDGE,"E61"),sQuery(id+"F0.wireOp",EDGE,"E63"),sQuery(id+"F0.wireOp",EDGE,"E65")])]});
            var Q54;
            Q54=makeQuery(id+"F1.opExtrude","SWEPT_BODY",BODY,{"disambiguationData":[OSD([sQuery(id+"F0.wireOp",EDGE,"E68"),sQuery(id+"F0.wireOp",EDGE,"E69"),sQuery(id+"F0.wireOp",EDGE,"E70"),sQuery(id+"F0.wireOp",EDGE,"E71"),sQuery(id+"F0.wireOp",EDGE,"E72"),sQuery(id+"F0.wireOp",EDGE,"E73"),sQuery(id+"F0.wireOp",EDGE,"E74"),sQuery(id+"F0.wireOp",EDGE,"E75"),sQuery(id+"F0.wireOp",EDGE,"E76"),sQuery(id+"F0.wireOp",EDGE,"E77"),sQuery(id+"F0.wireOp",EDGE,"E78"),sQuery(id+"F0.wireOp",EDGE,"E79"),sQuery(id+"F0.wireOp",EDGE,"E80"),sQuery(id+"F0.wireOp",EDGE,"E81"),sQuery(id+"F0.wireOp",EDGE,"E82"),sQuery(id+"F0.wireOp",EDGE,"E83")])]});
            var Q55;
            Q55=makeQuery(id+"F1.opExtrude","SWEPT_BODY",BODY,{"disambiguationData":[OSD([sQuery(id+"F0.wireOp",EDGE,"E86"),sQuery(id+"F0.wireOp",EDGE,"E89"),sQuery(id+"F0.wireOp",EDGE,"E90"),sQuery(id+"F0.wireOp",EDGE,"E91")])]});
            var Q56;
            Q56=makeQuery(id+"F1.opExtrude","SWEPT_BODY",BODY,{"disambiguationData":[OSD([sQuery(id+"F0.wireOp",EDGE,"E94"),sQuery(id+"F0.wireOp",EDGE,"E95"),sQuery(id+"F0.wireOp",EDGE,"E98"),sQuery(id+"F0.wireOp",EDGE,"E99")])]});
            var Q57;
            Q57=makeQuery(id+"F1.opExtrude","SWEPT_BODY",BODY,{"disambiguationData":[OSD([sQuery(id+"F0.wireOp",EDGE,"E102"),sQuery(id+"F0.wireOp",EDGE,"E103"),sQuery(id+"F0.wireOp",EDGE,"E104"),sQuery(id+"F0.wireOp",EDGE,"E105"),sQuery(id+"F0.wireOp",EDGE,"E106"),sQuery(id+"F0.wireOp",EDGE,"E107"),sQuery(id+"F0.wireOp",EDGE,"E108"),sQuery(id+"F0.wireOp",EDGE,"E109"),sQuery(id+"F0.wireOp",EDGE,"E110"),sQuery(id+"F0.wireOp",EDGE,"E111"),sQuery(id+"F0.wireOp",EDGE,"E112"),sQuery(id+"F0.wireOp",EDGE,"E113"),sQuery(id+"F0.wireOp",EDGE,"E114"),sQuery(id+"F0.wireOp",EDGE,"E115"),sQuery(id+"F0.wireOp",EDGE,"E116"),sQuery(id+"F0.wireOp",EDGE,"E117")])]});
            var Q58;
            Q58=makeQuery(id+"F1.opExtrude","SWEPT_BODY",BODY,{"disambiguationData":[OSD([sQuery(id+"F0.wireOp",EDGE,"E120"),sQuery(id+"F0.wireOp",EDGE,"E121"),sQuery(id+"F0.wireOp",EDGE,"E124"),sQuery(id+"F0.wireOp",EDGE,"E125")])]});
            deleteBodies(context, id + "F2", {"entities" : qUnion([Q0, Q1, Q2, Q3, Q4, Q5, Q6, Q7, Q8, Q9, Q10, Q11, Q12, Q13, Q14, Q15, Q16, Q17, Q18, Q19, Q20, Q21, Q22, Q23, Q24, Q25, Q26, Q27, Q28, Q29, Q30, Q31, Q32, Q33, Q34, Q35, Q36, Q37, Q38, Q39, Q40, Q41, Q42, Q43, Q44, Q45, Q46, Q47, Q48, Q49, Q50, Q51, Q52, Q53, Q54, Q55, Q56, Q57, Q58])});
        }
    });
